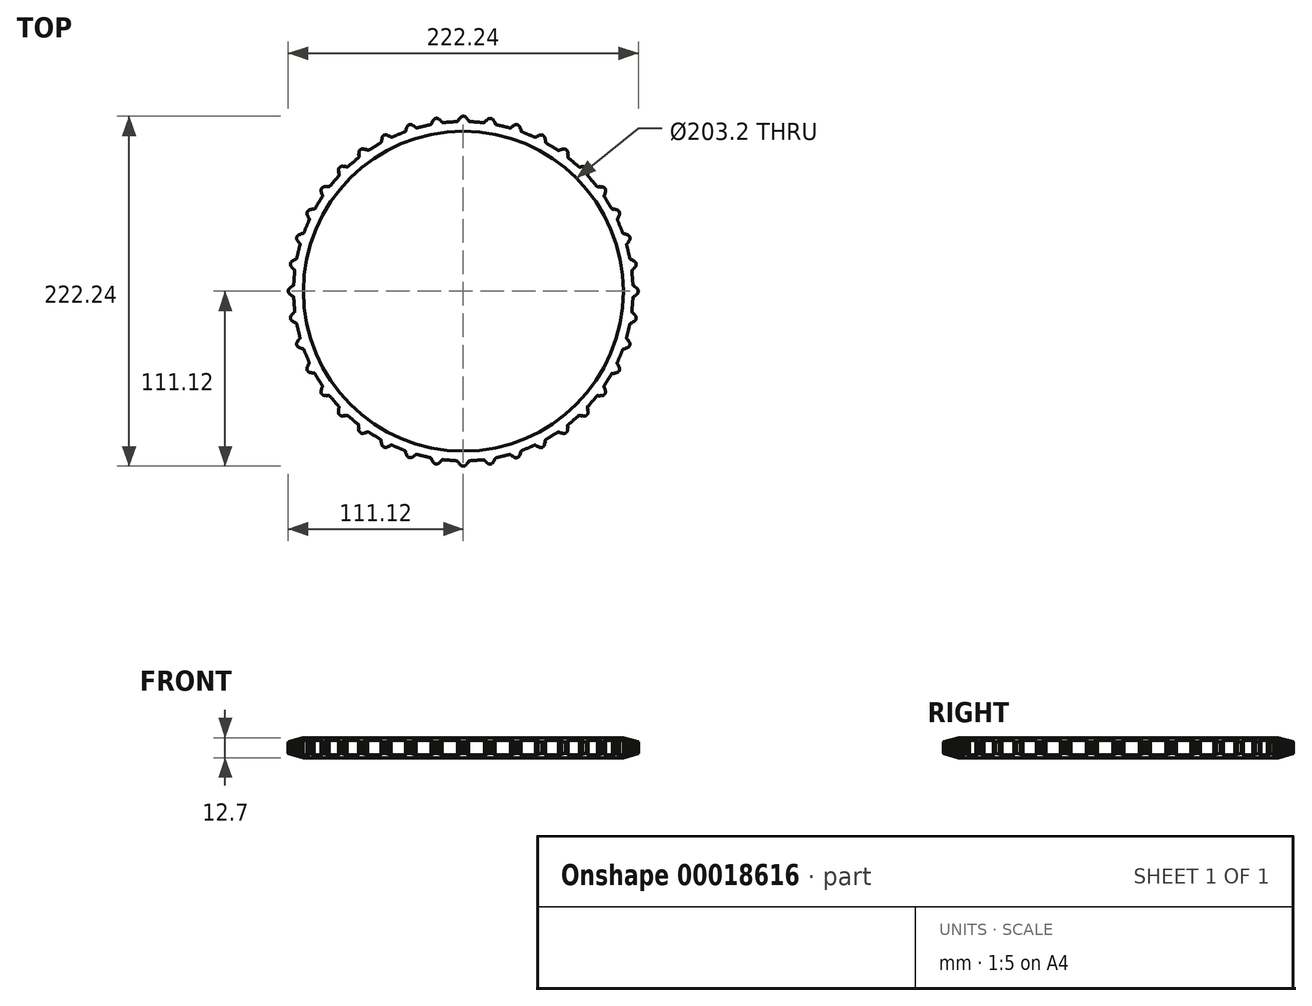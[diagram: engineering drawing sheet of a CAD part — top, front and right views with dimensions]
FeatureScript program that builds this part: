
annotation { "Feature Type Name" : "Feature", "Feature Type Description" : "" }
export const myFeature = defineFeature(function(context is Context, id is Id, definition is map)
    precondition{}
    {
        {
            var Q0;
            Q0=qCreatedBy(makeId("Top.planeOp"),FACE);
            var sketch = newSketch(context, id + "F0", { "sketchPlane" : qUnion([Q0])});
            skCircle(sketch, "E0", {"center": v(0, 0) * mm, "radius": 101.6 * mm});
            skCircle(sketch, "E1", {"center": v(0, 0) * mm, "radius": 111.13 * mm});
            skSolve(sketch);
        }
        {
            var Q0;
            Q0=qSketchRegion(id+"F0",true);
            extrude(context, id + "F1", {"entities" : qUnion([Q0]), "depth" : 12.7 * mm});
        }
        {
            var Q0;
            Q0=makeQuery(id+"F1.opExtrude","CAP_FACE",FACE,{"disambiguationData":[OSD([sQuery(id+"F0.wireOp",EDGE,"E0"),sQuery(id+"F0.wireOp",EDGE,"E1")])],"isStart":false});
            var sketch = newSketch(context, id + "F2", { "sketchPlane" : qUnion([Q0])});
            skLineSegment(sketch, "E2", {"start": v(0, 0) * mm, "end": v(0, 111.13) * mm, "construction": true});
            skArc(sketch, "E3", {"start": v(3.3, 108.7) * mm, "mid": v(2.05, 110.45) * mm, "end": v(0, 111.13) * mm});
            skCircle(sketch, "E4", {"center": v(0, 0) * mm, "radius": 107.95 * mm, "construction": true});
            skArc(sketch, "E5", {"start": v(8.83, 110.77) * mm, "mid": v(6.85, 110.27) * mm, "end": v(5.59, 108.66) * mm});
            skArc(sketch, "E6", {"start": v(3.3, 108.7) * mm, "mid": v(4.43, 107.86) * mm, "end": v(5.59, 108.66) * mm});
            skLineSegment(sketch, "E7", {"start": v(8.58, 107.6) * mm, "end": v(8.83, 110.77) * mm, "construction": true});
            skArc(sketch, "E8.1.0", {"start": v(-5.24, 108.63) * mm, "mid": v(-6.62, 110.27) * mm, "end": v(-8.72, 110.78) * mm});
            skArc(sketch, "E8.1.1", {"start": v(0.12, 111.12) * mm, "mid": v(-1.82, 110.47) * mm, "end": v(-2.96, 108.77) * mm});
            skArc(sketch, "E8.1.2", {"start": v(-5.24, 108.63) * mm, "mid": v(-4.05, 107.87) * mm, "end": v(-2.96, 108.77) * mm});
            skArc(sketch, "E8.2.0", {"start": v(-13.74, 107.88) * mm, "mid": v(-15.26, 109.41) * mm, "end": v(-17.38, 109.76) * mm});
            skArc(sketch, "E8.2.1", {"start": v(-8.6, 110.8) * mm, "mid": v(-10.48, 109.98) * mm, "end": v(-11.48, 108.2) * mm});
            skArc(sketch, "E8.2.2", {"start": v(-13.74, 107.88) * mm, "mid": v(-12.5, 107.22) * mm, "end": v(-11.48, 108.2) * mm});
            skArc(sketch, "E8.3.0", {"start": v(-22.16, 106.47) * mm, "mid": v(-23.8, 107.88) * mm, "end": v(-25.94, 108.05) * mm});
            skArc(sketch, "E8.3.1", {"start": v(-17.27, 109.77) * mm, "mid": v(-19.08, 108.82) * mm, "end": v(-19.93, 106.97) * mm});
            skArc(sketch, "E8.3.2", {"start": v(-22.16, 106.47) * mm, "mid": v(-20.87, 105.91) * mm, "end": v(-19.93, 106.97) * mm});
            skArc(sketch, "E8.4.0", {"start": v(-30.45, 104.4) * mm, "mid": v(-32.18, 105.68) * mm, "end": v(-34.34, 105.69) * mm});
            skArc(sketch, "E8.4.1", {"start": v(-25.83, 108.08) * mm, "mid": v(-27.56, 107) * mm, "end": v(-28.26, 105.07) * mm});
            skArc(sketch, "E8.4.2", {"start": v(-30.45, 104.4) * mm, "mid": v(-29.12, 103.95) * mm, "end": v(-28.26, 105.07) * mm});
            skArc(sketch, "E8.5.0", {"start": v(-38.55, 101.7) * mm, "mid": v(-40.38, 102.83) * mm, "end": v(-42.53, 102.67) * mm});
            skArc(sketch, "E8.5.1", {"start": v(-34.23, 105.72) * mm, "mid": v(-35.87, 104.5) * mm, "end": v(-36.42, 102.53) * mm});
            skArc(sketch, "E8.5.2", {"start": v(-38.55, 101.7) * mm, "mid": v(-37.18, 101.34) * mm, "end": v(-36.42, 102.53) * mm});
            skArc(sketch, "E8.6.0", {"start": v(-46.4, 98.35) * mm, "mid": v(-48.32, 99.35) * mm, "end": v(-50.45, 99.01) * mm});
            skArc(sketch, "E8.6.1", {"start": v(-42.42, 102.71) * mm, "mid": v(-43.96, 101.36) * mm, "end": v(-44.35, 99.36) * mm});
            skArc(sketch, "E8.6.2", {"start": v(-46.4, 98.35) * mm, "mid": v(-45.02, 98.12) * mm, "end": v(-44.35, 99.36) * mm});
            skArc(sketch, "E8.7.0", {"start": v(-53.98, 94.4) * mm, "mid": v(-55.97, 95.25) * mm, "end": v(-58.06, 94.75) * mm});
            skArc(sketch, "E8.7.1", {"start": v(-50.35, 99.07) * mm, "mid": v(-51.77, 97.6) * mm, "end": v(-52.01, 95.57) * mm});
            skArc(sketch, "E8.7.2", {"start": v(-53.98, 94.4) * mm, "mid": v(-52.58, 94.28) * mm, "end": v(-52.01, 95.57) * mm});
            skArc(sketch, "E8.8.0", {"start": v(-61.22, 89.88) * mm, "mid": v(-63.27, 90.56) * mm, "end": v(-65.32, 89.9) * mm});
            skArc(sketch, "E8.8.1", {"start": v(-57.96, 94.81) * mm, "mid": v(-59.27, 93.24) * mm, "end": v(-59.35, 91.2) * mm});
            skArc(sketch, "E8.8.2", {"start": v(-61.22, 89.88) * mm, "mid": v(-59.81, 89.86) * mm, "end": v(-59.35, 91.2) * mm});
            skArc(sketch, "E8.9.0", {"start": v(-68.09, 84.8) * mm, "mid": v(-70.18, 85.32) * mm, "end": v(-72.17, 84.5) * mm});
            skArc(sketch, "E8.9.1", {"start": v(-65.22, 89.97) * mm, "mid": v(-66.4, 88.3) * mm, "end": v(-66.32, 86.26) * mm});
            skArc(sketch, "E8.9.2", {"start": v(-68.09, 84.8) * mm, "mid": v(-66.68, 84.9) * mm, "end": v(-66.32, 86.26) * mm});
            skArc(sketch, "E8.10.0", {"start": v(-74.53, 79.2) * mm, "mid": v(-76.65, 79.55) * mm, "end": v(-78.58, 78.58) * mm});
            skArc(sketch, "E8.10.1", {"start": v(-72.08, 84.58) * mm, "mid": v(-73.13, 82.82) * mm, "end": v(-72.89, 80.79) * mm});
            skArc(sketch, "E8.10.2", {"start": v(-74.53, 79.2) * mm, "mid": v(-73.13, 79.4) * mm, "end": v(-72.89, 80.79) * mm});
            skArc(sketch, "E8.11.0", {"start": v(-80.51, 73.1) * mm, "mid": v(-82.66, 73.3) * mm, "end": v(-84.5, 72.17) * mm});
            skArc(sketch, "E8.11.1", {"start": v(-78.5, 78.66) * mm, "mid": v(-79.4, 76.83) * mm, "end": v(-79, 74.82) * mm});
            skArc(sketch, "E8.11.2", {"start": v(-80.51, 73.1) * mm, "mid": v(-79.14, 73.42) * mm, "end": v(-79, 74.82) * mm});
            skArc(sketch, "E8.12.0", {"start": v(-86, 66.57) * mm, "mid": v(-88.16, 66.58) * mm, "end": v(-89.9, 65.32) * mm});
            skArc(sketch, "E8.12.1", {"start": v(-84.42, 72.26) * mm, "mid": v(-85.18, 70.36) * mm, "end": v(-84.63, 68.4) * mm});
            skArc(sketch, "E8.12.2", {"start": v(-86, 66.57) * mm, "mid": v(-84.66, 66.98) * mm, "end": v(-84.63, 68.4) * mm});
            skArc(sketch, "E8.13.0", {"start": v(-90.96, 59.61) * mm, "mid": v(-93.1, 59.46) * mm, "end": v(-94.75, 58.06) * mm});
            skArc(sketch, "E8.13.1", {"start": v(-89.83, 65.41) * mm, "mid": v(-90.44, 63.46) * mm, "end": v(-89.73, 61.54) * mm});
            skArc(sketch, "E8.13.2", {"start": v(-90.96, 59.61) * mm, "mid": v(-89.65, 60.13) * mm, "end": v(-89.73, 61.54) * mm});
            skArc(sketch, "E8.14.0", {"start": v(-95.36, 52.3) * mm, "mid": v(-97.49, 51.97) * mm, "end": v(-99.01, 50.45) * mm});
            skArc(sketch, "E8.14.1", {"start": v(-94.69, 58.16) * mm, "mid": v(-95.14, 56.17) * mm, "end": v(-94.28, 54.31) * mm});
            skArc(sketch, "E8.14.2", {"start": v(-95.36, 52.3) * mm, "mid": v(-94.1, 52.92) * mm, "end": v(-94.28, 54.31) * mm});
            skArc(sketch, "E8.15.0", {"start": v(-99.16, 44.65) * mm, "mid": v(-101.26, 44.16) * mm, "end": v(-102.67, 42.53) * mm});
            skArc(sketch, "E8.15.1", {"start": v(-98.96, 50.55) * mm, "mid": v(-99.25, 48.53) * mm, "end": v(-98.25, 46.75) * mm});
            skArc(sketch, "E8.15.2", {"start": v(-99.16, 44.65) * mm, "mid": v(-97.95, 45.37) * mm, "end": v(-98.25, 46.75) * mm});
            skArc(sketch, "E8.16.0", {"start": v(-102.36, 36.73) * mm, "mid": v(-104.42, 36.08) * mm, "end": v(-105.69, 34.34) * mm});
            skArc(sketch, "E8.16.1", {"start": v(-102.62, 42.63) * mm, "mid": v(-102.76, 40.6) * mm, "end": v(-101.62, 38.9) * mm});
            skArc(sketch, "E8.16.2", {"start": v(-102.36, 36.73) * mm, "mid": v(-101.21, 37.54) * mm, "end": v(-101.62, 38.9) * mm});
            skArc(sketch, "E8.17.0", {"start": v(-104.93, 28.59) * mm, "mid": v(-106.92, 27.78) * mm, "end": v(-108.05, 25.94) * mm});
            skArc(sketch, "E8.17.1", {"start": v(-105.65, 34.45) * mm, "mid": v(-105.62, 32.4) * mm, "end": v(-104.36, 30.8) * mm});
            skArc(sketch, "E8.17.2", {"start": v(-104.93, 28.59) * mm, "mid": v(-103.84, 29.49) * mm, "end": v(-104.36, 30.8) * mm});
            skArc(sketch, "E8.18.0", {"start": v(-106.85, 20.27) * mm, "mid": v(-108.77, 19.3) * mm, "end": v(-109.76, 17.38) * mm});
            skArc(sketch, "E8.18.1", {"start": v(-108.03, 26.05) * mm, "mid": v(-107.84, 24.02) * mm, "end": v(-106.45, 22.52) * mm});
            skArc(sketch, "E8.18.2", {"start": v(-106.85, 20.27) * mm, "mid": v(-105.84, 21.25) * mm, "end": v(-106.45, 22.52) * mm});
            skArc(sketch, "E8.19.0", {"start": v(-108.1, 11.82) * mm, "mid": v(-109.95, 10.7) * mm, "end": v(-110.78, 8.72) * mm});
            skArc(sketch, "E8.19.1", {"start": v(-109.74, 17.5) * mm, "mid": v(-109.4, 15.48) * mm, "end": v(-107.9, 14.1) * mm});
            skArc(sketch, "E8.19.2", {"start": v(-108.1, 11.82) * mm, "mid": v(-107.18, 12.88) * mm, "end": v(-107.9, 14.1) * mm});
            skArc(sketch, "E8.20.0", {"start": v(-108.7, 3.3) * mm, "mid": v(-110.45, 2.05) * mm, "end": v(-111.13, 0) * mm});
            skArc(sketch, "E8.20.1", {"start": v(-110.77, 8.83) * mm, "mid": v(-110.27, 6.85) * mm, "end": v(-108.66, 5.59) * mm});
            skArc(sketch, "E8.20.2", {"start": v(-108.7, 3.3) * mm, "mid": v(-107.86, 4.43) * mm, "end": v(-108.66, 5.59) * mm});
            skArc(sketch, "E8.21.0", {"start": v(-108.63, -5.24) * mm, "mid": v(-110.27, -6.62) * mm, "end": v(-110.78, -8.72) * mm});
            skArc(sketch, "E8.21.1", {"start": v(-111.12, 0.12) * mm, "mid": v(-110.47, -1.82) * mm, "end": v(-108.77, -2.96) * mm});
            skArc(sketch, "E8.21.2", {"start": v(-108.63, -5.24) * mm, "mid": v(-107.87, -4.05) * mm, "end": v(-108.77, -2.96) * mm});
            skArc(sketch, "E8.22.0", {"start": v(-107.88, -13.74) * mm, "mid": v(-109.41, -15.26) * mm, "end": v(-109.76, -17.38) * mm});
            skArc(sketch, "E8.22.1", {"start": v(-110.8, -8.6) * mm, "mid": v(-109.98, -10.48) * mm, "end": v(-108.2, -11.48) * mm});
            skArc(sketch, "E8.22.2", {"start": v(-107.88, -13.74) * mm, "mid": v(-107.22, -12.5) * mm, "end": v(-108.2, -11.48) * mm});
            skArc(sketch, "E8.23.0", {"start": v(-106.47, -22.16) * mm, "mid": v(-107.88, -23.8) * mm, "end": v(-108.05, -25.94) * mm});
            skArc(sketch, "E8.23.1", {"start": v(-109.77, -17.27) * mm, "mid": v(-108.82, -19.08) * mm, "end": v(-106.97, -19.93) * mm});
            skArc(sketch, "E8.23.2", {"start": v(-106.47, -22.16) * mm, "mid": v(-105.91, -20.87) * mm, "end": v(-106.97, -19.93) * mm});
            skArc(sketch, "E8.24.0", {"start": v(-104.4, -30.45) * mm, "mid": v(-105.68, -32.18) * mm, "end": v(-105.69, -34.34) * mm});
            skArc(sketch, "E8.24.1", {"start": v(-108.08, -25.83) * mm, "mid": v(-107, -27.56) * mm, "end": v(-105.07, -28.26) * mm});
            skArc(sketch, "E8.24.2", {"start": v(-104.4, -30.45) * mm, "mid": v(-103.95, -29.12) * mm, "end": v(-105.07, -28.26) * mm});
            skArc(sketch, "E8.25.0", {"start": v(-101.7, -38.55) * mm, "mid": v(-102.83, -40.38) * mm, "end": v(-102.67, -42.53) * mm});
            skArc(sketch, "E8.25.1", {"start": v(-105.72, -34.23) * mm, "mid": v(-104.5, -35.87) * mm, "end": v(-102.53, -36.42) * mm});
            skArc(sketch, "E8.25.2", {"start": v(-101.7, -38.55) * mm, "mid": v(-101.34, -37.18) * mm, "end": v(-102.53, -36.42) * mm});
            skArc(sketch, "E8.26.0", {"start": v(-98.35, -46.4) * mm, "mid": v(-99.35, -48.32) * mm, "end": v(-99.01, -50.45) * mm});
            skArc(sketch, "E8.26.1", {"start": v(-102.71, -42.42) * mm, "mid": v(-101.36, -43.96) * mm, "end": v(-99.36, -44.35) * mm});
            skArc(sketch, "E8.26.2", {"start": v(-98.35, -46.4) * mm, "mid": v(-98.12, -45.02) * mm, "end": v(-99.36, -44.35) * mm});
            skArc(sketch, "E8.27.0", {"start": v(-94.4, -53.98) * mm, "mid": v(-95.25, -55.97) * mm, "end": v(-94.75, -58.06) * mm});
            skArc(sketch, "E8.27.1", {"start": v(-99.07, -50.35) * mm, "mid": v(-97.6, -51.77) * mm, "end": v(-95.57, -52.01) * mm});
            skArc(sketch, "E8.27.2", {"start": v(-94.4, -53.98) * mm, "mid": v(-94.28, -52.58) * mm, "end": v(-95.57, -52.01) * mm});
            skArc(sketch, "E8.28.0", {"start": v(-89.88, -61.22) * mm, "mid": v(-90.56, -63.27) * mm, "end": v(-89.9, -65.32) * mm});
            skArc(sketch, "E8.28.1", {"start": v(-94.81, -57.96) * mm, "mid": v(-93.24, -59.27) * mm, "end": v(-91.2, -59.35) * mm});
            skArc(sketch, "E8.28.2", {"start": v(-89.88, -61.22) * mm, "mid": v(-89.86, -59.81) * mm, "end": v(-91.2, -59.35) * mm});
            skArc(sketch, "E8.29.0", {"start": v(-84.8, -68.09) * mm, "mid": v(-85.32, -70.18) * mm, "end": v(-84.5, -72.17) * mm});
            skArc(sketch, "E8.29.1", {"start": v(-89.97, -65.22) * mm, "mid": v(-88.3, -66.4) * mm, "end": v(-86.26, -66.32) * mm});
            skArc(sketch, "E8.29.2", {"start": v(-84.8, -68.09) * mm, "mid": v(-84.9, -66.68) * mm, "end": v(-86.26, -66.32) * mm});
            skArc(sketch, "E8.30.0", {"start": v(-79.2, -74.53) * mm, "mid": v(-79.55, -76.65) * mm, "end": v(-78.58, -78.58) * mm});
            skArc(sketch, "E8.30.1", {"start": v(-84.58, -72.08) * mm, "mid": v(-82.82, -73.13) * mm, "end": v(-80.79, -72.89) * mm});
            skArc(sketch, "E8.30.2", {"start": v(-79.2, -74.53) * mm, "mid": v(-79.4, -73.13) * mm, "end": v(-80.79, -72.89) * mm});
            skArc(sketch, "E8.31.0", {"start": v(-73.1, -80.51) * mm, "mid": v(-73.3, -82.66) * mm, "end": v(-72.17, -84.5) * mm});
            skArc(sketch, "E8.31.1", {"start": v(-78.66, -78.5) * mm, "mid": v(-76.83, -79.4) * mm, "end": v(-74.82, -79) * mm});
            skArc(sketch, "E8.31.2", {"start": v(-73.1, -80.51) * mm, "mid": v(-73.42, -79.14) * mm, "end": v(-74.82, -79) * mm});
            skArc(sketch, "E8.32.0", {"start": v(-66.57, -86) * mm, "mid": v(-66.58, -88.16) * mm, "end": v(-65.32, -89.9) * mm});
            skArc(sketch, "E8.32.1", {"start": v(-72.26, -84.42) * mm, "mid": v(-70.36, -85.18) * mm, "end": v(-68.4, -84.63) * mm});
            skArc(sketch, "E8.32.2", {"start": v(-66.57, -86) * mm, "mid": v(-66.98, -84.66) * mm, "end": v(-68.4, -84.63) * mm});
            skArc(sketch, "E8.33.0", {"start": v(-59.61, -90.96) * mm, "mid": v(-59.46, -93.1) * mm, "end": v(-58.06, -94.75) * mm});
            skArc(sketch, "E8.33.1", {"start": v(-65.41, -89.83) * mm, "mid": v(-63.46, -90.44) * mm, "end": v(-61.54, -89.73) * mm});
            skArc(sketch, "E8.33.2", {"start": v(-59.61, -90.96) * mm, "mid": v(-60.13, -89.65) * mm, "end": v(-61.54, -89.73) * mm});
            skArc(sketch, "E8.34.0", {"start": v(-52.3, -95.36) * mm, "mid": v(-51.97, -97.49) * mm, "end": v(-50.45, -99.01) * mm});
            skArc(sketch, "E8.34.1", {"start": v(-58.16, -94.69) * mm, "mid": v(-56.17, -95.14) * mm, "end": v(-54.31, -94.28) * mm});
            skArc(sketch, "E8.34.2", {"start": v(-52.3, -95.36) * mm, "mid": v(-52.92, -94.1) * mm, "end": v(-54.31, -94.28) * mm});
            skArc(sketch, "E8.35.0", {"start": v(-44.65, -99.16) * mm, "mid": v(-44.16, -101.26) * mm, "end": v(-42.53, -102.67) * mm});
            skArc(sketch, "E8.35.1", {"start": v(-50.55, -98.96) * mm, "mid": v(-48.53, -99.25) * mm, "end": v(-46.75, -98.25) * mm});
            skArc(sketch, "E8.35.2", {"start": v(-44.65, -99.16) * mm, "mid": v(-45.37, -97.95) * mm, "end": v(-46.75, -98.25) * mm});
            skArc(sketch, "E8.36.0", {"start": v(-36.73, -102.36) * mm, "mid": v(-36.08, -104.42) * mm, "end": v(-34.34, -105.69) * mm});
            skArc(sketch, "E8.36.1", {"start": v(-42.63, -102.62) * mm, "mid": v(-40.6, -102.76) * mm, "end": v(-38.9, -101.62) * mm});
            skArc(sketch, "E8.36.2", {"start": v(-36.73, -102.36) * mm, "mid": v(-37.54, -101.21) * mm, "end": v(-38.9, -101.62) * mm});
            skArc(sketch, "E8.37.0", {"start": v(-28.59, -104.93) * mm, "mid": v(-27.78, -106.92) * mm, "end": v(-25.94, -108.05) * mm});
            skArc(sketch, "E8.37.1", {"start": v(-34.45, -105.65) * mm, "mid": v(-32.4, -105.62) * mm, "end": v(-30.8, -104.36) * mm});
            skArc(sketch, "E8.37.2", {"start": v(-28.59, -104.93) * mm, "mid": v(-29.49, -103.84) * mm, "end": v(-30.8, -104.36) * mm});
            skArc(sketch, "E8.38.0", {"start": v(-20.27, -106.85) * mm, "mid": v(-19.3, -108.77) * mm, "end": v(-17.38, -109.76) * mm});
            skArc(sketch, "E8.38.1", {"start": v(-26.05, -108.03) * mm, "mid": v(-24.02, -107.84) * mm, "end": v(-22.52, -106.45) * mm});
            skArc(sketch, "E8.38.2", {"start": v(-20.27, -106.85) * mm, "mid": v(-21.25, -105.84) * mm, "end": v(-22.52, -106.45) * mm});
            skArc(sketch, "E8.39.0", {"start": v(-11.82, -108.1) * mm, "mid": v(-10.7, -109.95) * mm, "end": v(-8.72, -110.78) * mm});
            skArc(sketch, "E8.39.1", {"start": v(-17.5, -109.74) * mm, "mid": v(-15.48, -109.4) * mm, "end": v(-14.1, -107.9) * mm});
            skArc(sketch, "E8.39.2", {"start": v(-11.82, -108.1) * mm, "mid": v(-12.88, -107.18) * mm, "end": v(-14.1, -107.9) * mm});
            skArc(sketch, "E8.40.0", {"start": v(-3.3, -108.7) * mm, "mid": v(-2.05, -110.45) * mm, "end": v(0, -111.13) * mm});
            skArc(sketch, "E8.40.1", {"start": v(-8.83, -110.77) * mm, "mid": v(-6.85, -110.27) * mm, "end": v(-5.59, -108.66) * mm});
            skArc(sketch, "E8.40.2", {"start": v(-3.3, -108.7) * mm, "mid": v(-4.43, -107.86) * mm, "end": v(-5.59, -108.66) * mm});
            skArc(sketch, "E8.41.0", {"start": v(5.24, -108.63) * mm, "mid": v(6.62, -110.27) * mm, "end": v(8.72, -110.78) * mm});
            skArc(sketch, "E8.41.1", {"start": v(-0.12, -111.12) * mm, "mid": v(1.82, -110.47) * mm, "end": v(2.96, -108.77) * mm});
            skArc(sketch, "E8.41.2", {"start": v(5.24, -108.63) * mm, "mid": v(4.05, -107.87) * mm, "end": v(2.96, -108.77) * mm});
            skArc(sketch, "E8.42.0", {"start": v(13.74, -107.88) * mm, "mid": v(15.26, -109.41) * mm, "end": v(17.38, -109.76) * mm});
            skArc(sketch, "E8.42.1", {"start": v(8.6, -110.8) * mm, "mid": v(10.48, -109.98) * mm, "end": v(11.48, -108.2) * mm});
            skArc(sketch, "E8.42.2", {"start": v(13.74, -107.88) * mm, "mid": v(12.5, -107.22) * mm, "end": v(11.48, -108.2) * mm});
            skArc(sketch, "E8.43.0", {"start": v(22.16, -106.47) * mm, "mid": v(23.8, -107.88) * mm, "end": v(25.94, -108.05) * mm});
            skArc(sketch, "E8.43.1", {"start": v(17.27, -109.77) * mm, "mid": v(19.08, -108.82) * mm, "end": v(19.93, -106.97) * mm});
            skArc(sketch, "E8.43.2", {"start": v(22.16, -106.47) * mm, "mid": v(20.87, -105.91) * mm, "end": v(19.93, -106.97) * mm});
            skArc(sketch, "E8.44.0", {"start": v(30.45, -104.4) * mm, "mid": v(32.18, -105.68) * mm, "end": v(34.34, -105.69) * mm});
            skArc(sketch, "E8.44.1", {"start": v(25.83, -108.08) * mm, "mid": v(27.56, -107) * mm, "end": v(28.26, -105.07) * mm});
            skArc(sketch, "E8.44.2", {"start": v(30.45, -104.4) * mm, "mid": v(29.12, -103.95) * mm, "end": v(28.26, -105.07) * mm});
            skArc(sketch, "E8.45.0", {"start": v(38.55, -101.7) * mm, "mid": v(40.38, -102.83) * mm, "end": v(42.53, -102.67) * mm});
            skArc(sketch, "E8.45.1", {"start": v(34.23, -105.72) * mm, "mid": v(35.87, -104.5) * mm, "end": v(36.42, -102.53) * mm});
            skArc(sketch, "E8.45.2", {"start": v(38.55, -101.7) * mm, "mid": v(37.18, -101.34) * mm, "end": v(36.42, -102.53) * mm});
            skArc(sketch, "E8.46.0", {"start": v(46.4, -98.35) * mm, "mid": v(48.32, -99.35) * mm, "end": v(50.45, -99.01) * mm});
            skArc(sketch, "E8.46.1", {"start": v(42.42, -102.71) * mm, "mid": v(43.96, -101.36) * mm, "end": v(44.35, -99.36) * mm});
            skArc(sketch, "E8.46.2", {"start": v(46.4, -98.35) * mm, "mid": v(45.02, -98.12) * mm, "end": v(44.35, -99.36) * mm});
            skArc(sketch, "E8.47.0", {"start": v(53.98, -94.4) * mm, "mid": v(55.97, -95.25) * mm, "end": v(58.06, -94.75) * mm});
            skArc(sketch, "E8.47.1", {"start": v(50.35, -99.07) * mm, "mid": v(51.77, -97.6) * mm, "end": v(52.01, -95.57) * mm});
            skArc(sketch, "E8.47.2", {"start": v(53.98, -94.4) * mm, "mid": v(52.58, -94.28) * mm, "end": v(52.01, -95.57) * mm});
            skArc(sketch, "E8.48.0", {"start": v(61.22, -89.88) * mm, "mid": v(63.27, -90.56) * mm, "end": v(65.32, -89.9) * mm});
            skArc(sketch, "E8.48.1", {"start": v(57.96, -94.81) * mm, "mid": v(59.27, -93.24) * mm, "end": v(59.35, -91.2) * mm});
            skArc(sketch, "E8.48.2", {"start": v(61.22, -89.88) * mm, "mid": v(59.81, -89.86) * mm, "end": v(59.35, -91.2) * mm});
            skArc(sketch, "E8.49.0", {"start": v(68.09, -84.8) * mm, "mid": v(70.18, -85.32) * mm, "end": v(72.17, -84.5) * mm});
            skArc(sketch, "E8.49.1", {"start": v(65.22, -89.97) * mm, "mid": v(66.4, -88.3) * mm, "end": v(66.32, -86.26) * mm});
            skArc(sketch, "E8.49.2", {"start": v(68.09, -84.8) * mm, "mid": v(66.68, -84.9) * mm, "end": v(66.32, -86.26) * mm});
            skArc(sketch, "E8.50.0", {"start": v(74.53, -79.2) * mm, "mid": v(76.65, -79.55) * mm, "end": v(78.58, -78.58) * mm});
            skArc(sketch, "E8.50.1", {"start": v(72.08, -84.58) * mm, "mid": v(73.13, -82.82) * mm, "end": v(72.89, -80.79) * mm});
            skArc(sketch, "E8.50.2", {"start": v(74.53, -79.2) * mm, "mid": v(73.13, -79.4) * mm, "end": v(72.89, -80.79) * mm});
            skArc(sketch, "E8.51.0", {"start": v(80.51, -73.1) * mm, "mid": v(82.66, -73.3) * mm, "end": v(84.5, -72.17) * mm});
            skArc(sketch, "E8.51.1", {"start": v(78.5, -78.66) * mm, "mid": v(79.4, -76.83) * mm, "end": v(79, -74.82) * mm});
            skArc(sketch, "E8.51.2", {"start": v(80.51, -73.1) * mm, "mid": v(79.14, -73.42) * mm, "end": v(79, -74.82) * mm});
            skArc(sketch, "E8.52.0", {"start": v(86, -66.57) * mm, "mid": v(88.16, -66.58) * mm, "end": v(89.9, -65.32) * mm});
            skArc(sketch, "E8.52.1", {"start": v(84.42, -72.26) * mm, "mid": v(85.18, -70.36) * mm, "end": v(84.63, -68.4) * mm});
            skArc(sketch, "E8.52.2", {"start": v(86, -66.57) * mm, "mid": v(84.66, -66.98) * mm, "end": v(84.63, -68.4) * mm});
            skArc(sketch, "E8.53.0", {"start": v(90.96, -59.61) * mm, "mid": v(93.1, -59.46) * mm, "end": v(94.75, -58.06) * mm});
            skArc(sketch, "E8.53.1", {"start": v(89.83, -65.41) * mm, "mid": v(90.44, -63.46) * mm, "end": v(89.73, -61.54) * mm});
            skArc(sketch, "E8.53.2", {"start": v(90.96, -59.61) * mm, "mid": v(89.65, -60.13) * mm, "end": v(89.73, -61.54) * mm});
            skArc(sketch, "E8.54.0", {"start": v(95.36, -52.3) * mm, "mid": v(97.49, -51.97) * mm, "end": v(99.01, -50.45) * mm});
            skArc(sketch, "E8.54.1", {"start": v(94.69, -58.16) * mm, "mid": v(95.14, -56.17) * mm, "end": v(94.28, -54.31) * mm});
            skArc(sketch, "E8.54.2", {"start": v(95.36, -52.3) * mm, "mid": v(94.1, -52.92) * mm, "end": v(94.28, -54.31) * mm});
            skArc(sketch, "E8.55.0", {"start": v(99.16, -44.65) * mm, "mid": v(101.26, -44.16) * mm, "end": v(102.67, -42.53) * mm});
            skArc(sketch, "E8.55.1", {"start": v(98.96, -50.55) * mm, "mid": v(99.25, -48.53) * mm, "end": v(98.25, -46.75) * mm});
            skArc(sketch, "E8.55.2", {"start": v(99.16, -44.65) * mm, "mid": v(97.95, -45.37) * mm, "end": v(98.25, -46.75) * mm});
            skArc(sketch, "E8.56.0", {"start": v(102.36, -36.73) * mm, "mid": v(104.42, -36.08) * mm, "end": v(105.69, -34.34) * mm});
            skArc(sketch, "E8.56.1", {"start": v(102.62, -42.63) * mm, "mid": v(102.76, -40.6) * mm, "end": v(101.62, -38.9) * mm});
            skArc(sketch, "E8.56.2", {"start": v(102.36, -36.73) * mm, "mid": v(101.21, -37.54) * mm, "end": v(101.62, -38.9) * mm});
            skArc(sketch, "E8.57.0", {"start": v(104.93, -28.59) * mm, "mid": v(106.92, -27.78) * mm, "end": v(108.05, -25.94) * mm});
            skArc(sketch, "E8.57.1", {"start": v(105.65, -34.45) * mm, "mid": v(105.62, -32.4) * mm, "end": v(104.36, -30.8) * mm});
            skArc(sketch, "E8.57.2", {"start": v(104.93, -28.59) * mm, "mid": v(103.84, -29.49) * mm, "end": v(104.36, -30.8) * mm});
            skArc(sketch, "E8.58.0", {"start": v(106.85, -20.27) * mm, "mid": v(108.77, -19.3) * mm, "end": v(109.76, -17.38) * mm});
            skArc(sketch, "E8.58.1", {"start": v(108.03, -26.05) * mm, "mid": v(107.84, -24.02) * mm, "end": v(106.45, -22.52) * mm});
            skArc(sketch, "E8.58.2", {"start": v(106.85, -20.27) * mm, "mid": v(105.84, -21.25) * mm, "end": v(106.45, -22.52) * mm});
            skArc(sketch, "E8.59.0", {"start": v(108.1, -11.82) * mm, "mid": v(109.95, -10.7) * mm, "end": v(110.78, -8.72) * mm});
            skArc(sketch, "E8.59.1", {"start": v(109.74, -17.5) * mm, "mid": v(109.4, -15.48) * mm, "end": v(107.9, -14.1) * mm});
            skArc(sketch, "E8.59.2", {"start": v(108.1, -11.82) * mm, "mid": v(107.18, -12.88) * mm, "end": v(107.9, -14.1) * mm});
            skArc(sketch, "E8.60.0", {"start": v(108.7, -3.3) * mm, "mid": v(110.45, -2.05) * mm, "end": v(111.13, 0) * mm});
            skArc(sketch, "E8.60.1", {"start": v(110.77, -8.83) * mm, "mid": v(110.27, -6.85) * mm, "end": v(108.66, -5.59) * mm});
            skArc(sketch, "E8.60.2", {"start": v(108.7, -3.3) * mm, "mid": v(107.86, -4.43) * mm, "end": v(108.66, -5.59) * mm});
            skArc(sketch, "E8.61.0", {"start": v(108.63, 5.24) * mm, "mid": v(110.27, 6.62) * mm, "end": v(110.78, 8.72) * mm});
            skArc(sketch, "E8.61.1", {"start": v(111.12, -0.12) * mm, "mid": v(110.47, 1.82) * mm, "end": v(108.77, 2.96) * mm});
            skArc(sketch, "E8.61.2", {"start": v(108.63, 5.24) * mm, "mid": v(107.87, 4.05) * mm, "end": v(108.77, 2.96) * mm});
            skArc(sketch, "E8.62.0", {"start": v(107.88, 13.74) * mm, "mid": v(109.41, 15.26) * mm, "end": v(109.76, 17.38) * mm});
            skArc(sketch, "E8.62.1", {"start": v(110.8, 8.6) * mm, "mid": v(109.98, 10.48) * mm, "end": v(108.2, 11.48) * mm});
            skArc(sketch, "E8.62.2", {"start": v(107.88, 13.74) * mm, "mid": v(107.22, 12.5) * mm, "end": v(108.2, 11.48) * mm});
            skArc(sketch, "E8.63.0", {"start": v(106.47, 22.16) * mm, "mid": v(107.88, 23.8) * mm, "end": v(108.05, 25.94) * mm});
            skArc(sketch, "E8.63.1", {"start": v(109.77, 17.27) * mm, "mid": v(108.82, 19.08) * mm, "end": v(106.97, 19.93) * mm});
            skArc(sketch, "E8.63.2", {"start": v(106.47, 22.16) * mm, "mid": v(105.91, 20.87) * mm, "end": v(106.97, 19.93) * mm});
            skArc(sketch, "E8.64.0", {"start": v(104.4, 30.45) * mm, "mid": v(105.68, 32.18) * mm, "end": v(105.69, 34.34) * mm});
            skArc(sketch, "E8.64.1", {"start": v(108.08, 25.83) * mm, "mid": v(107, 27.56) * mm, "end": v(105.07, 28.26) * mm});
            skArc(sketch, "E8.64.2", {"start": v(104.4, 30.45) * mm, "mid": v(103.95, 29.12) * mm, "end": v(105.07, 28.26) * mm});
            skArc(sketch, "E8.65.0", {"start": v(101.7, 38.55) * mm, "mid": v(102.83, 40.38) * mm, "end": v(102.67, 42.53) * mm});
            skArc(sketch, "E8.65.1", {"start": v(105.72, 34.23) * mm, "mid": v(104.5, 35.87) * mm, "end": v(102.53, 36.42) * mm});
            skArc(sketch, "E8.65.2", {"start": v(101.7, 38.55) * mm, "mid": v(101.34, 37.18) * mm, "end": v(102.53, 36.42) * mm});
            skArc(sketch, "E8.66.0", {"start": v(98.35, 46.4) * mm, "mid": v(99.35, 48.32) * mm, "end": v(99.01, 50.45) * mm});
            skArc(sketch, "E8.66.1", {"start": v(102.71, 42.42) * mm, "mid": v(101.36, 43.96) * mm, "end": v(99.36, 44.35) * mm});
            skArc(sketch, "E8.66.2", {"start": v(98.35, 46.4) * mm, "mid": v(98.12, 45.02) * mm, "end": v(99.36, 44.35) * mm});
            skArc(sketch, "E8.67.0", {"start": v(94.4, 53.98) * mm, "mid": v(95.25, 55.97) * mm, "end": v(94.75, 58.06) * mm});
            skArc(sketch, "E8.67.1", {"start": v(99.07, 50.35) * mm, "mid": v(97.6, 51.77) * mm, "end": v(95.57, 52.01) * mm});
            skArc(sketch, "E8.67.2", {"start": v(94.4, 53.98) * mm, "mid": v(94.28, 52.58) * mm, "end": v(95.57, 52.01) * mm});
            skArc(sketch, "E8.68.0", {"start": v(89.88, 61.22) * mm, "mid": v(90.56, 63.27) * mm, "end": v(89.9, 65.32) * mm});
            skArc(sketch, "E8.68.1", {"start": v(94.81, 57.96) * mm, "mid": v(93.24, 59.27) * mm, "end": v(91.2, 59.35) * mm});
            skArc(sketch, "E8.68.2", {"start": v(89.88, 61.22) * mm, "mid": v(89.86, 59.81) * mm, "end": v(91.2, 59.35) * mm});
            skArc(sketch, "E8.69.0", {"start": v(84.8, 68.09) * mm, "mid": v(85.32, 70.18) * mm, "end": v(84.5, 72.17) * mm});
            skArc(sketch, "E8.69.1", {"start": v(89.97, 65.22) * mm, "mid": v(88.3, 66.4) * mm, "end": v(86.26, 66.32) * mm});
            skArc(sketch, "E8.69.2", {"start": v(84.8, 68.09) * mm, "mid": v(84.9, 66.68) * mm, "end": v(86.26, 66.32) * mm});
            skArc(sketch, "E8.70.0", {"start": v(79.2, 74.53) * mm, "mid": v(79.55, 76.65) * mm, "end": v(78.58, 78.58) * mm});
            skArc(sketch, "E8.70.1", {"start": v(84.58, 72.08) * mm, "mid": v(82.82, 73.13) * mm, "end": v(80.79, 72.89) * mm});
            skArc(sketch, "E8.70.2", {"start": v(79.2, 74.53) * mm, "mid": v(79.4, 73.13) * mm, "end": v(80.79, 72.89) * mm});
            skArc(sketch, "E8.71.0", {"start": v(73.1, 80.51) * mm, "mid": v(73.3, 82.66) * mm, "end": v(72.17, 84.5) * mm});
            skArc(sketch, "E8.71.1", {"start": v(78.66, 78.5) * mm, "mid": v(76.83, 79.4) * mm, "end": v(74.82, 79) * mm});
            skArc(sketch, "E8.71.2", {"start": v(73.1, 80.51) * mm, "mid": v(73.42, 79.14) * mm, "end": v(74.82, 79) * mm});
            skArc(sketch, "E8.72.0", {"start": v(66.57, 86) * mm, "mid": v(66.58, 88.16) * mm, "end": v(65.32, 89.9) * mm});
            skArc(sketch, "E8.72.1", {"start": v(72.26, 84.42) * mm, "mid": v(70.36, 85.18) * mm, "end": v(68.4, 84.63) * mm});
            skArc(sketch, "E8.72.2", {"start": v(66.57, 86) * mm, "mid": v(66.98, 84.66) * mm, "end": v(68.4, 84.63) * mm});
            skArc(sketch, "E8.73.0", {"start": v(59.61, 90.96) * mm, "mid": v(59.46, 93.1) * mm, "end": v(58.06, 94.75) * mm});
            skArc(sketch, "E8.73.1", {"start": v(65.41, 89.83) * mm, "mid": v(63.46, 90.44) * mm, "end": v(61.54, 89.73) * mm});
            skArc(sketch, "E8.73.2", {"start": v(59.61, 90.96) * mm, "mid": v(60.13, 89.65) * mm, "end": v(61.54, 89.73) * mm});
            skArc(sketch, "E8.74.0", {"start": v(52.3, 95.36) * mm, "mid": v(51.97, 97.49) * mm, "end": v(50.45, 99.01) * mm});
            skArc(sketch, "E8.74.1", {"start": v(58.16, 94.69) * mm, "mid": v(56.17, 95.14) * mm, "end": v(54.31, 94.28) * mm});
            skArc(sketch, "E8.74.2", {"start": v(52.3, 95.36) * mm, "mid": v(52.92, 94.1) * mm, "end": v(54.31, 94.28) * mm});
            skArc(sketch, "E8.75.0", {"start": v(44.65, 99.16) * mm, "mid": v(44.16, 101.26) * mm, "end": v(42.53, 102.67) * mm});
            skArc(sketch, "E8.75.1", {"start": v(50.55, 98.96) * mm, "mid": v(48.53, 99.25) * mm, "end": v(46.75, 98.25) * mm});
            skArc(sketch, "E8.75.2", {"start": v(44.65, 99.16) * mm, "mid": v(45.37, 97.95) * mm, "end": v(46.75, 98.25) * mm});
            skArc(sketch, "E8.76.0", {"start": v(36.73, 102.36) * mm, "mid": v(36.08, 104.42) * mm, "end": v(34.34, 105.69) * mm});
            skArc(sketch, "E8.76.1", {"start": v(42.63, 102.62) * mm, "mid": v(40.6, 102.76) * mm, "end": v(38.9, 101.62) * mm});
            skArc(sketch, "E8.76.2", {"start": v(36.73, 102.36) * mm, "mid": v(37.54, 101.21) * mm, "end": v(38.9, 101.62) * mm});
            skArc(sketch, "E8.77.0", {"start": v(28.59, 104.93) * mm, "mid": v(27.78, 106.92) * mm, "end": v(25.94, 108.05) * mm});
            skArc(sketch, "E8.77.1", {"start": v(34.45, 105.65) * mm, "mid": v(32.4, 105.62) * mm, "end": v(30.8, 104.36) * mm});
            skArc(sketch, "E8.77.2", {"start": v(28.59, 104.93) * mm, "mid": v(29.49, 103.84) * mm, "end": v(30.8, 104.36) * mm});
            skArc(sketch, "E8.78.0", {"start": v(20.27, 106.85) * mm, "mid": v(19.3, 108.77) * mm, "end": v(17.38, 109.76) * mm});
            skArc(sketch, "E8.78.1", {"start": v(26.05, 108.03) * mm, "mid": v(24.02, 107.84) * mm, "end": v(22.52, 106.45) * mm});
            skArc(sketch, "E8.78.2", {"start": v(20.27, 106.85) * mm, "mid": v(21.25, 105.84) * mm, "end": v(22.52, 106.45) * mm});
            skArc(sketch, "E8.79.0", {"start": v(11.82, 108.1) * mm, "mid": v(10.7, 109.95) * mm, "end": v(8.72, 110.78) * mm});
            skArc(sketch, "E8.79.1", {"start": v(17.5, 109.74) * mm, "mid": v(15.48, 109.4) * mm, "end": v(14.1, 107.9) * mm});
            skArc(sketch, "E8.79.2", {"start": v(11.82, 108.1) * mm, "mid": v(12.88, 107.18) * mm, "end": v(14.1, 107.9) * mm});
            skCircle(sketch, "E9", {"center": v(0, 0) * mm, "radius": 129.3 * mm});
            skSolve(sketch);
        }
        {
            var Q0;
            Q0=qSketchRegion(id+"F2",true);
            extrude(context, id + "F3", {"entities" : qUnion([Q0]), "operationType" : NewBodyOperationType.REMOVE, "oppositeDirection" : true, "depth" : 25.4 * mm});
        }
        {
            var Q0;
            Q0=qCreatedBy(makeId("Top.planeOp"),FACE);
            var sketch = newSketch(context, id + "F4", { "sketchPlane" : qUnion([Q0])});
            skCircle(sketch, "E10", {"center": v(0, 0) * mm, "radius": 106.71 * mm});
            skSolve(sketch);
        }
        {
            var Q0;
            Q0=qSketchRegion(id+"F4",true);
            extrude(context, id + "F5", {"entities" : qUnion([Q0]), "depth" : 19.05 * mm, "hasSecondDirection" : true, "secondDirectionOppositeDirection" : true, "secondDirectionDepth" : 6.35 * mm});
        }
        {
            var Q0;
            Q0=makeQuery(id+"F5.opExtrude","CAP_EDGE",EDGE,{"disambiguationData":[OSD([sQuery(id+"F4.wireOp",EDGE,"E10")])],"isStart":false});
            var Q1;
            Q1=makeQuery(id+"F5.opExtrude","CAP_EDGE",EDGE,{"disambiguationData":[OSD([sQuery(id+"F4.wireOp",EDGE,"E10")])],"isStart":true});
            fillet(context, id + "F6", {"entities" : qUnion([Q0, Q1]), "radius" : 6.35 * mm, "tangentPropagation" : true, "allowEdgeOverflow" : false});
        }
        {
            var Q0;
            Q0=makeQuery(id+"F5.opExtrude","CAP_FACE",FACE,{"disambiguationData":[OSD([sQuery(id+"F4.wireOp",EDGE,"E10")])],"isStart":false});
            var sketch = newSketch(context, id + "F7", { "sketchPlane" : qUnion([Q0])});
            skArc(sketch, "E11", {"start": v(-85.48, 42.02) * mm, "mid": v(-95.25, 0) * mm, "end": v(-85.48, -42.02) * mm});
            skLineSegment(sketch, "E12.rect.left", {"start": v(6.35, 95.04) * mm, "end": v(6.35, 17.96) * mm});
            skLineSegment(sketch, "E12.rect.right", {"start": v(-6.35, 95.04) * mm, "end": v(-6.35, 17.96) * mm});
            skPoint(sketch, "E12.rect.top.end.orphan", {"position": v(-6.35, -100.16) * mm});
            skPoint(sketch, "E13.trimOffspring.end.orphan", {"position": v(6.35, -100.16) * mm});
            skPoint(sketch, "E14.orphan", {"position": v(6.35, 100.16) * mm});
            skPoint(sketch, "E15.orphan", {"position": v(-6.35, 100.16) * mm});
            skLineSegment(sketch, "E16.1.0", {"start": v(-85.48, 42.02) * mm, "end": v(-18.73, 3.48) * mm});
            skLineSegment(sketch, "E16.1.2", {"start": v(-79.13, 53.02) * mm, "end": v(-12.38, 14.48) * mm});
            skPoint(sketch, "E16.1.3", {"position": v(-89.92, 44.58) * mm});
            skPoint(sketch, "E16.1.4", {"position": v(-83.57, 55.58) * mm});
            skLineSegment(sketch, "E16.2.0", {"start": v(-79.13, -53.02) * mm, "end": v(-12.38, -14.48) * mm});
            skLineSegment(sketch, "E16.2.2", {"start": v(-85.48, -42.02) * mm, "end": v(-18.73, -3.48) * mm});
            skPoint(sketch, "E16.2.3", {"position": v(-83.57, -55.58) * mm});
            skPoint(sketch, "E16.2.4", {"position": v(-89.92, -44.58) * mm});
            skLineSegment(sketch, "E16.3.0", {"start": v(6.35, -95.04) * mm, "end": v(6.35, -17.96) * mm});
            skLineSegment(sketch, "E16.3.2", {"start": v(-6.35, -95.04) * mm, "end": v(-6.35, -17.96) * mm});
            skLineSegment(sketch, "E16.4.0", {"start": v(85.48, -42.02) * mm, "end": v(18.73, -3.48) * mm});
            skLineSegment(sketch, "E16.4.2", {"start": v(79.13, -53.02) * mm, "end": v(12.38, -14.48) * mm});
            skPoint(sketch, "E16.4.3", {"position": v(89.92, -44.58) * mm});
            skPoint(sketch, "E16.4.4", {"position": v(83.57, -55.58) * mm});
            skLineSegment(sketch, "E16.5.0", {"start": v(79.13, 53.02) * mm, "end": v(12.38, 14.48) * mm});
            skLineSegment(sketch, "E16.5.2", {"start": v(85.48, 42.02) * mm, "end": v(18.73, 3.48) * mm});
            skPoint(sketch, "E16.5.3", {"position": v(83.57, 55.58) * mm});
            skPoint(sketch, "E16.5.4", {"position": v(89.92, 44.58) * mm});
            skArc(sketch, "E17", {"start": v(-12.38, -14.48) * mm, "mid": v(-9.52, -16.5) * mm, "end": v(-6.35, -17.96) * mm});
            skArc(sketch, "E18.trimOffspring", {"start": v(-6.35, 95.04) * mm, "mid": v(-47.62, 82.49) * mm, "end": v(-79.13, 53.02) * mm});
            skArc(sketch, "E19.trimOffspring", {"start": v(79.13, 53.02) * mm, "mid": v(47.63, 82.49) * mm, "end": v(6.35, 95.04) * mm});
            skArc(sketch, "E20.trimOffspring", {"start": v(85.48, -42.02) * mm, "mid": v(95.25, 0) * mm, "end": v(85.48, 42.02) * mm});
            skArc(sketch, "E21.trimOffspring", {"start": v(6.35, -95.04) * mm, "mid": v(47.62, -82.49) * mm, "end": v(79.13, -53.02) * mm});
            skArc(sketch, "E22.trimOffspring", {"start": v(-79.13, -53.02) * mm, "mid": v(-47.63, -82.49) * mm, "end": v(-6.35, -95.04) * mm});
            skPoint(sketch, "E23.trimOffspring.end.orphan", {"position": v(-6.35, 0) * mm});
            skPoint(sketch, "E24.orphan", {"position": v(3.18, 5.5) * mm});
            skArc(sketch, "E25.trimOffspring", {"start": v(-18.73, 3.48) * mm, "mid": v(-19.05, 0) * mm, "end": v(-18.73, -3.48) * mm});
            skArc(sketch, "E26.trimOffspring", {"start": v(-6.35, 17.96) * mm, "mid": v(-9.52, 16.5) * mm, "end": v(-12.38, 14.48) * mm});
            skArc(sketch, "E27.trimOffspring", {"start": v(12.38, 14.48) * mm, "mid": v(9.53, 16.5) * mm, "end": v(6.35, 17.96) * mm});
            skPoint(sketch, "E28.orphan", {"position": v(6.35, 0) * mm});
            skArc(sketch, "E29.trimOffspring", {"start": v(6.35, -17.96) * mm, "mid": v(9.52, -16.5) * mm, "end": v(12.38, -14.48) * mm});
            skArc(sketch, "E30.trimOffspring", {"start": v(18.73, -3.48) * mm, "mid": v(19.05, 0) * mm, "end": v(18.73, 3.48) * mm});
            skSolve(sketch);
        }
        {
            var Q0;
            Q0=qSketchRegion(id+"F7",true);
            extrude(context, id + "F8", {"entities" : qUnion([Q0]), "operationType" : NewBodyOperationType.REMOVE, "endBound" : BoundingType.THROUGH_ALL, "oppositeDirection" : true, "depth" : 25.4 * mm});
        }
        {
            var Q0;
            Q0=makeQuery(id+"F5.opExtrude","CAP_FACE",FACE,{"disambiguationData":[OSD([sQuery(id+"F4.wireOp",EDGE,"E10")])],"isStart":false});
            var sketch = newSketch(context, id + "F9", { "sketchPlane" : qUnion([Q0])});
            skCircle(sketch, "E31", {"center": v(0, 0) * mm, "radius": 6.35 * mm});
            skSolve(sketch);
        }
        {
            var Q0;
            Q0=qSketchRegion(id+"F9",true);
            extrude(context, id + "F10", {"entities" : qUnion([Q0]), "operationType" : NewBodyOperationType.REMOVE, "endBound" : BoundingType.THROUGH_ALL, "oppositeDirection" : true, "depth" : 25.4 * mm});
        }
        {
            var Q0;
            Q0=makeQuery(id+"F5.opExtrude","SWEPT_BODY",BODY,{"disambiguationData":[OSD([sQuery(id+"F4.wireOp",EDGE,"E10")])]});
            deleteBodies(context, id + "F11", {"entities" : qUnion([Q0])});
        }
        {
            var Q0;
            Q0=qCreatedBy(makeId("Right.planeOp"),FACE);
            var sketch = newSketch(context, id + "F12", { "sketchPlane" : qUnion([Q0])});
            skLineSegment(sketch, "E32", {"start": v(-113.32, 3.36) * mm, "end": v(-113.32, 9.34) * mm});
            skLineSegment(sketch, "E33", {"start": v(-113.32, 9.34) * mm, "end": v(-101.6, 12.7) * mm});
            skLineSegment(sketch, "E34", {"start": v(-101.6, 0) * mm, "end": v(-113.32, 3.36) * mm});
            skLineSegment(sketch, "E35", {"start": v(-101.6, 0) * mm, "end": v(-101.6, 0) * mm});
            skLineSegment(sketch, "E36", {"start": v(-101.6, 0) * mm, "end": v(-119.44, 0) * mm});
            skLineSegment(sketch, "E37", {"start": v(-119.44, 0) * mm, "end": v(-119.44, 12.7) * mm});
            skLineSegment(sketch, "E38", {"start": v(-119.44, 12.7) * mm, "end": v(-101.6, 12.7) * mm});
            skLineSegment(sketch, "E39", {"start": v(0, 0) * mm, "end": v(0, -54.5) * mm, "construction": true});
            skSolve(sketch);
        }
        {
            var Q0;
            Q0=qSketchRegion(id+"F12",true);
            var Q1;
            Q1=sQuery(id+"F12.wireOp",EDGE,"E39");
            revolve(context, id + "F13", {"operationType" : NewBodyOperationType.REMOVE, "entities" : qUnion([Q0]), "axis" : qUnion([Q1]), "revolveType" : RevolveType.FULL, "oppositeDirection" : true});
        }
        {
            var Q0;
            Q0=qCreatedBy(makeId("Top.planeOp"),FACE);
            var sketch = newSketch(context, id + "F14", { "sketchPlane" : qUnion([Q0])});
            skLineSegment(sketch, "E40", {"start": v(0, 0) * mm, "end": v(-15.83, 202.58) * mm, "construction": true});
            skLineSegment(sketch, "E41.bottom", {"start": v(0, 111.12) * mm, "end": v(-8.36, 110.47) * mm, "construction": true});
            skLineSegment(sketch, "E42", {"start": v(0, 0) * mm, "end": v(0, 118.5) * mm, "construction": true});
            skLineSegment(sketch, "E43", {"start": v(0, 111.12) * mm, "end": v(-9.22, 118) * mm});
            skPoint(sketch, "E44.MirrorCS.end.orphan", {"position": v(-9.22, 118) * mm});
            skPoint(sketch, "E45.center", {"position": v(0, 0) * mm});
            skArc(sketch, "E46.MirrorCS", {"start": v(-3.98, 107.75) * mm, "mid": v(-3.69, 107.83) * mm, "end": v(-3.45, 108.02) * mm});
            skLineSegment(sketch, "E47.MirrorCS", {"start": v(-8.54, 107.4) * mm, "end": v(-3.98, 107.75) * mm});
            skArc(sketch, "E48", {"start": v(0, 111.12) * mm, "mid": v(-1.46, 110.62) * mm, "end": v(-2.3, 109.33) * mm});
            skLineSegment(sketch, "E49", {"start": v(-2.3, 109.33) * mm, "end": v(-2.3, 109.33) * mm});
            skPoint(sketch, "E50.trimOffspring.end.orphan", {"position": v(-1.5, 110.55) * mm});
            skLineSegment(sketch, "E51.MirrorCS", {"start": v(-14.7, 108.36) * mm, "end": v(-14.73, 108.36) * mm});
            skPoint(sketch, "E52.center", {"position": v(0.06, -0.13) * mm});
            skLineSegment(sketch, "E53", {"start": v(-2.3, 109.33) * mm, "end": v(-2.73, 109.33) * mm});
            skLineSegment(sketch, "E54", {"start": v(-2.73, 109.33) * mm, "end": v(-3.45, 108.02) * mm});
            skArc(sketch, "E55.MirrorCS", {"start": v(-17.27, 109.77) * mm, "mid": v(-15.75, 109.5) * mm, "end": v(-14.7, 108.36) * mm});
            skLineSegment(sketch, "E56.MirrorCS", {"start": v(-14.73, 108.36) * mm, "end": v(-14.3, 108.43) * mm});
            skArc(sketch, "E57.MirrorCS", {"start": v(-12.81, 107.06) * mm, "mid": v(-13.11, 107.1) * mm, "end": v(-13.38, 107.24) * mm});
            skLineSegment(sketch, "E58.MirrorCS", {"start": v(-14.3, 108.43) * mm, "end": v(-13.38, 107.24) * mm});
            skLineSegment(sketch, "E59.MirrorCS", {"start": v(-17.27, 109.77) * mm, "end": v(-9.22, 118) * mm});
            skLineSegment(sketch, "E60.MirrorCS", {"start": v(-8.25, 107.42) * mm, "end": v(-12.81, 107.06) * mm});
            skLineSegment(sketch, "E61.1.0", {"start": v(-34.23, 105.72) * mm, "end": v(-27.57, 115.11) * mm});
            skLineSegment(sketch, "E61.1.1", {"start": v(-17.38, 109.75) * mm, "end": v(-27.57, 115.11) * mm});
            skLineSegment(sketch, "E61.1.2", {"start": v(-24.95, 104.8) * mm, "end": v(-29.4, 103.74) * mm});
            skLineSegment(sketch, "E61.1.3", {"start": v(-31.08, 104.86) * mm, "end": v(-30, 103.83) * mm});
            skArc(sketch, "E61.1.4", {"start": v(-29.4, 103.74) * mm, "mid": v(-29.7, 103.73) * mm, "end": v(-30, 103.83) * mm});
            skLineSegment(sketch, "E61.1.5", {"start": v(-31.5, 104.72) * mm, "end": v(-31.08, 104.86) * mm});
            skArc(sketch, "E61.1.6", {"start": v(-34.23, 105.72) * mm, "mid": v(-32.68, 105.7) * mm, "end": v(-31.48, 104.73) * mm});
            skLineSegment(sketch, "E61.1.7", {"start": v(-31.48, 104.73) * mm, "end": v(-31.5, 104.72) * mm});
            skLineSegment(sketch, "E61.1.8", {"start": v(-31.48, 104.73) * mm, "end": v(-31.5, 104.72) * mm});
            skArc(sketch, "E61.1.9", {"start": v(-20.79, 105.8) * mm, "mid": v(-20.5, 105.93) * mm, "end": v(-20.3, 106.15) * mm});
            skLineSegment(sketch, "E61.1.10", {"start": v(-25.24, 104.74) * mm, "end": v(-20.79, 105.8) * mm});
            skLineSegment(sketch, "E61.1.11", {"start": v(-19.8, 107.56) * mm, "end": v(-20.3, 106.15) * mm});
            skArc(sketch, "E61.1.12", {"start": v(-17.38, 109.75) * mm, "mid": v(-18.75, 109.03) * mm, "end": v(-19.38, 107.63) * mm});
            skLineSegment(sketch, "E61.1.13", {"start": v(-19.37, 107.63) * mm, "end": v(-19.8, 107.56) * mm});
            skLineSegment(sketch, "E61.2.0", {"start": v(-50.34, 99.07) * mm, "end": v(-45.24, 109.38) * mm});
            skLineSegment(sketch, "E61.2.1", {"start": v(-34.34, 105.68) * mm, "end": v(-45.24, 109.38) * mm});
            skLineSegment(sketch, "E61.2.2", {"start": v(-41.04, 99.61) * mm, "end": v(-45.27, 97.86) * mm});
            skLineSegment(sketch, "E61.2.3", {"start": v(-47.1, 98.7) * mm, "end": v(-45.87, 97.86) * mm});
            skArc(sketch, "E61.2.4", {"start": v(-45.27, 97.86) * mm, "mid": v(-45.57, 97.8) * mm, "end": v(-45.87, 97.86) * mm});
            skLineSegment(sketch, "E61.2.5", {"start": v(-47.5, 98.5) * mm, "end": v(-47.1, 98.7) * mm});
            skArc(sketch, "E61.2.6", {"start": v(-50.34, 99.07) * mm, "mid": v(-48.81, 99.28) * mm, "end": v(-47.48, 98.51) * mm});
            skLineSegment(sketch, "E61.2.7", {"start": v(-47.48, 98.51) * mm, "end": v(-47.5, 98.5) * mm});
            skLineSegment(sketch, "E61.2.8", {"start": v(-47.48, 98.51) * mm, "end": v(-47.5, 98.5) * mm});
            skArc(sketch, "E61.2.9", {"start": v(-37.08, 101.25) * mm, "mid": v(-36.83, 101.42) * mm, "end": v(-36.66, 101.67) * mm});
            skLineSegment(sketch, "E61.2.10", {"start": v(-41.31, 99.5) * mm, "end": v(-37.08, 101.25) * mm});
            skLineSegment(sketch, "E61.2.11", {"start": v(-36.38, 103.14) * mm, "end": v(-36.66, 101.67) * mm});
            skArc(sketch, "E61.2.12", {"start": v(-34.34, 105.68) * mm, "mid": v(-35.57, 104.76) * mm, "end": v(-35.98, 103.27) * mm});
            skLineSegment(sketch, "E61.2.13", {"start": v(-35.96, 103.27) * mm, "end": v(-36.38, 103.14) * mm});
            skLineSegment(sketch, "E61.3.0", {"start": v(-65.22, 89.97) * mm, "end": v(-61.8, 100.96) * mm});
            skLineSegment(sketch, "E61.3.1", {"start": v(-50.45, 99.01) * mm, "end": v(-61.8, 100.96) * mm});
            skLineSegment(sketch, "E61.3.2", {"start": v(-56.12, 91.97) * mm, "end": v(-60.02, 89.58) * mm});
            skLineSegment(sketch, "E61.3.3", {"start": v(-61.96, 90.12) * mm, "end": v(-60.6, 89.48) * mm});
            skArc(sketch, "E61.3.4", {"start": v(-60.02, 89.58) * mm, "mid": v(-60.3, 89.47) * mm, "end": v(-60.6, 89.48) * mm});
            skLineSegment(sketch, "E61.3.5", {"start": v(-62.32, 89.86) * mm, "end": v(-61.96, 90.12) * mm});
            skArc(sketch, "E61.3.6", {"start": v(-65.22, 89.97) * mm, "mid": v(-63.74, 90.42) * mm, "end": v(-62.3, 89.87) * mm});
            skLineSegment(sketch, "E61.3.7", {"start": v(-62.3, 89.87) * mm, "end": v(-62.32, 89.86) * mm});
            skLineSegment(sketch, "E61.3.8", {"start": v(-62.3, 89.87) * mm, "end": v(-62.32, 89.86) * mm});
            skArc(sketch, "E61.3.9", {"start": v(-52.46, 94.2) * mm, "mid": v(-52.24, 94.4) * mm, "end": v(-52.1, 94.68) * mm});
            skLineSegment(sketch, "E61.3.10", {"start": v(-56.37, 91.81) * mm, "end": v(-52.46, 94.2) * mm});
            skLineSegment(sketch, "E61.3.11", {"start": v(-52.07, 96.18) * mm, "end": v(-52.1, 94.68) * mm});
            skArc(sketch, "E61.3.12", {"start": v(-50.45, 99.01) * mm, "mid": v(-51.52, 97.9) * mm, "end": v(-51.7, 96.37) * mm});
            skLineSegment(sketch, "E61.3.13", {"start": v(-51.68, 96.38) * mm, "end": v(-52.07, 96.18) * mm});
            skLineSegment(sketch, "E61.4.0", {"start": v(-78.5, 78.66) * mm, "end": v(-76.83, 90.05) * mm});
            skLineSegment(sketch, "E61.4.1", {"start": v(-65.32, 89.9) * mm, "end": v(-76.83, 90.05) * mm});
            skLineSegment(sketch, "E61.4.2", {"start": v(-69.81, 82.06) * mm, "end": v(-73.3, 79.08) * mm});
            skLineSegment(sketch, "E61.4.3", {"start": v(-75.3, 79.32) * mm, "end": v(-73.86, 78.9) * mm});
            skArc(sketch, "E61.4.4", {"start": v(-73.3, 79.08) * mm, "mid": v(-73.56, 78.94) * mm, "end": v(-73.86, 78.9) * mm});
            skLineSegment(sketch, "E61.4.5", {"start": v(-75.6, 79) * mm, "end": v(-75.3, 79.32) * mm});
            skArc(sketch, "E61.4.6", {"start": v(-78.5, 78.66) * mm, "mid": v(-77.1, 79.34) * mm, "end": v(-75.6, 79.02) * mm});
            skLineSegment(sketch, "E61.4.7", {"start": v(-75.6, 79.02) * mm, "end": v(-75.6, 79) * mm});
            skLineSegment(sketch, "E61.4.8", {"start": v(-75.6, 79.02) * mm, "end": v(-75.6, 79) * mm});
            skArc(sketch, "E61.4.9", {"start": v(-66.55, 84.83) * mm, "mid": v(-66.37, 85.07) * mm, "end": v(-66.28, 85.36) * mm});
            skLineSegment(sketch, "E61.4.10", {"start": v(-70.04, 81.86) * mm, "end": v(-66.55, 84.83) * mm});
            skLineSegment(sketch, "E61.4.11", {"start": v(-66.47, 86.85) * mm, "end": v(-66.28, 85.36) * mm});
            skArc(sketch, "E61.4.12", {"start": v(-65.32, 89.9) * mm, "mid": v(-66.2, 88.64) * mm, "end": v(-66.13, 87.1) * mm});
            skLineSegment(sketch, "E61.4.13", {"start": v(-66.12, 87.1) * mm, "end": v(-66.47, 86.85) * mm});
            skLineSegment(sketch, "E61.5.0", {"start": v(-89.83, 65.41) * mm, "end": v(-89.97, 76.92) * mm});
            skLineSegment(sketch, "E61.5.1", {"start": v(-78.58, 78.58) * mm, "end": v(-89.97, 76.92) * mm});
            skLineSegment(sketch, "E61.5.2", {"start": v(-81.79, 70.13) * mm, "end": v(-84.76, 66.65) * mm});
            skLineSegment(sketch, "E61.5.3", {"start": v(-86.78, 66.56) * mm, "end": v(-85.3, 66.37) * mm});
            skArc(sketch, "E61.5.4", {"start": v(-84.76, 66.65) * mm, "mid": v(-85, 66.46) * mm, "end": v(-85.3, 66.37) * mm});
            skLineSegment(sketch, "E61.5.5", {"start": v(-87.03, 66.2) * mm, "end": v(-86.78, 66.56) * mm});
            skArc(sketch, "E61.5.6", {"start": v(-89.83, 65.41) * mm, "mid": v(-88.57, 66.3) * mm, "end": v(-87.03, 66.22) * mm});
            skLineSegment(sketch, "E61.5.7", {"start": v(-87.03, 66.22) * mm, "end": v(-87.03, 66.2) * mm});
            skLineSegment(sketch, "E61.5.8", {"start": v(-87.03, 66.22) * mm, "end": v(-87.03, 66.2) * mm});
            skArc(sketch, "E61.5.9", {"start": v(-79, 73.38) * mm, "mid": v(-78.86, 73.64) * mm, "end": v(-78.82, 73.95) * mm});
            skLineSegment(sketch, "E61.5.10", {"start": v(-81.98, 69.9) * mm, "end": v(-79, 73.38) * mm});
            skLineSegment(sketch, "E61.5.11", {"start": v(-79.24, 75.38) * mm, "end": v(-78.82, 73.95) * mm});
            skArc(sketch, "E61.5.12", {"start": v(-78.58, 78.58) * mm, "mid": v(-79.25, 77.19) * mm, "end": v(-78.94, 75.68) * mm});
            skLineSegment(sketch, "E61.5.13", {"start": v(-78.93, 75.7) * mm, "end": v(-79.24, 75.38) * mm});
            skLineSegment(sketch, "E61.6.0", {"start": v(-98.96, 50.55) * mm, "end": v(-100.9, 61.9) * mm});
            skLineSegment(sketch, "E61.6.1", {"start": v(-89.9, 65.32) * mm, "end": v(-100.9, 61.9) * mm});
            skLineSegment(sketch, "E61.6.2", {"start": v(-91.75, 56.47) * mm, "end": v(-94.15, 52.56) * mm});
            skLineSegment(sketch, "E61.6.3", {"start": v(-96.12, 52.17) * mm, "end": v(-94.63, 52.21) * mm});
            skArc(sketch, "E61.6.4", {"start": v(-94.15, 52.56) * mm, "mid": v(-94.35, 52.34) * mm, "end": v(-94.63, 52.21) * mm});
            skLineSegment(sketch, "E61.6.5", {"start": v(-96.32, 51.78) * mm, "end": v(-96.12, 52.17) * mm});
            skArc(sketch, "E61.6.6", {"start": v(-98.96, 50.55) * mm, "mid": v(-97.85, 51.63) * mm, "end": v(-96.31, 51.8) * mm});
            skLineSegment(sketch, "E61.6.7", {"start": v(-96.31, 51.8) * mm, "end": v(-96.32, 51.78) * mm});
            skLineSegment(sketch, "E61.6.8", {"start": v(-96.31, 51.8) * mm, "end": v(-96.32, 51.78) * mm});
            skArc(sketch, "E61.6.9", {"start": v(-89.51, 60.12) * mm, "mid": v(-89.4, 60.4) * mm, "end": v(-89.41, 60.7) * mm});
            skLineSegment(sketch, "E61.6.10", {"start": v(-91.9, 56.21) * mm, "end": v(-89.51, 60.12) * mm});
            skLineSegment(sketch, "E61.6.11", {"start": v(-90.06, 62.06) * mm, "end": v(-89.41, 60.7) * mm});
            skArc(sketch, "E61.6.12", {"start": v(-89.9, 65.32) * mm, "mid": v(-90.35, 63.84) * mm, "end": v(-89.8, 62.4) * mm});
            skLineSegment(sketch, "E61.6.13", {"start": v(-89.8, 62.41) * mm, "end": v(-90.06, 62.06) * mm});
            skLineSegment(sketch, "E61.7.0", {"start": v(-105.65, 34.45) * mm, "end": v(-109.33, 45.36) * mm});
            skLineSegment(sketch, "E61.7.1", {"start": v(-99.01, 50.45) * mm, "end": v(-109.33, 45.36) * mm});
            skLineSegment(sketch, "E61.7.2", {"start": v(-99.46, 41.42) * mm, "end": v(-101.2, 37.2) * mm});
            skLineSegment(sketch, "E61.7.3", {"start": v(-103.1, 36.5) * mm, "end": v(-101.63, 36.77) * mm});
            skArc(sketch, "E61.7.4", {"start": v(-101.2, 37.2) * mm, "mid": v(-101.38, 36.94) * mm, "end": v(-101.63, 36.77) * mm});
            skLineSegment(sketch, "E61.7.5", {"start": v(-103.24, 36.07) * mm, "end": v(-103.1, 36.5) * mm});
            skArc(sketch, "E61.7.6", {"start": v(-105.65, 34.45) * mm, "mid": v(-104.72, 35.68) * mm, "end": v(-103.23, 36.09) * mm});
            skLineSegment(sketch, "E61.7.7", {"start": v(-103.23, 36.09) * mm, "end": v(-103.24, 36.07) * mm});
            skLineSegment(sketch, "E61.7.8", {"start": v(-103.23, 36.09) * mm, "end": v(-103.24, 36.07) * mm});
            skArc(sketch, "E61.7.9", {"start": v(-97.82, 45.37) * mm, "mid": v(-97.75, 45.67) * mm, "end": v(-97.81, 45.97) * mm});
            skLineSegment(sketch, "E61.7.10", {"start": v(-99.57, 41.14) * mm, "end": v(-97.82, 45.37) * mm});
            skLineSegment(sketch, "E61.7.11", {"start": v(-98.65, 47.2) * mm, "end": v(-97.81, 45.97) * mm});
            skArc(sketch, "E61.7.12", {"start": v(-99.01, 50.45) * mm, "mid": v(-99.23, 48.92) * mm, "end": v(-98.46, 47.58) * mm});
            skLineSegment(sketch, "E61.7.13", {"start": v(-98.46, 47.6) * mm, "end": v(-98.65, 47.2) * mm});
            skLineSegment(sketch, "E61.8.0", {"start": v(-109.74, 17.5) * mm, "end": v(-115.08, 27.7) * mm});
            skLineSegment(sketch, "E61.8.1", {"start": v(-105.68, 34.34) * mm, "end": v(-115.08, 27.7) * mm});
            skLineSegment(sketch, "E61.8.2", {"start": v(-104.71, 25.35) * mm, "end": v(-105.78, 20.9) * mm});
            skLineSegment(sketch, "E61.8.3", {"start": v(-107.54, 19.91) * mm, "end": v(-106.13, 20.41) * mm});
            skArc(sketch, "E61.8.4", {"start": v(-105.78, 20.9) * mm, "mid": v(-105.9, 20.62) * mm, "end": v(-106.13, 20.41) * mm});
            skLineSegment(sketch, "E61.8.5", {"start": v(-107.6, 19.48) * mm, "end": v(-107.54, 19.91) * mm});
            skArc(sketch, "E61.8.6", {"start": v(-109.74, 17.5) * mm, "mid": v(-109.01, 18.86) * mm, "end": v(-107.6, 19.5) * mm});
            skLineSegment(sketch, "E61.8.7", {"start": v(-107.6, 19.5) * mm, "end": v(-107.6, 19.48) * mm});
            skLineSegment(sketch, "E61.8.8", {"start": v(-107.6, 19.5) * mm, "end": v(-107.6, 19.48) * mm});
            skArc(sketch, "E61.8.9", {"start": v(-103.7, 29.51) * mm, "mid": v(-103.7, 29.82) * mm, "end": v(-103.8, 30.1) * mm});
            skLineSegment(sketch, "E61.8.10", {"start": v(-104.78, 25.06) * mm, "end": v(-103.7, 29.51) * mm});
            skLineSegment(sketch, "E61.8.11", {"start": v(-104.82, 31.2) * mm, "end": v(-103.8, 30.1) * mm});
            skArc(sketch, "E61.8.12", {"start": v(-105.68, 34.34) * mm, "mid": v(-105.66, 32.8) * mm, "end": v(-104.7, 31.6) * mm});
            skLineSegment(sketch, "E61.8.13", {"start": v(-104.69, 31.6) * mm, "end": v(-104.82, 31.2) * mm});
            skLineSegment(sketch, "E61.9.0", {"start": v(-111.12, 0.12) * mm, "end": v(-118, 9.35) * mm});
            skLineSegment(sketch, "E61.9.1", {"start": v(-109.75, 17.38) * mm, "end": v(-118, 9.35) * mm});
            skLineSegment(sketch, "E61.9.2", {"start": v(-107.39, 8.66) * mm, "end": v(-107.75, 4.1) * mm});
            skLineSegment(sketch, "E61.9.3", {"start": v(-109.33, 2.85) * mm, "end": v(-108.02, 3.56) * mm});
            skArc(sketch, "E61.9.4", {"start": v(-107.75, 4.1) * mm, "mid": v(-107.83, 3.8) * mm, "end": v(-108.02, 3.56) * mm});
            skLineSegment(sketch, "E61.9.5", {"start": v(-109.33, 2.4) * mm, "end": v(-109.33, 2.85) * mm});
            skArc(sketch, "E61.9.6", {"start": v(-111.12, 0.12) * mm, "mid": v(-110.62, 1.58) * mm, "end": v(-109.33, 2.42) * mm});
            skLineSegment(sketch, "E61.9.7", {"start": v(-109.33, 2.42) * mm, "end": v(-109.33, 2.4) * mm});
            skLineSegment(sketch, "E61.9.8", {"start": v(-109.33, 2.42) * mm, "end": v(-109.33, 2.4) * mm});
            skArc(sketch, "E61.9.9", {"start": v(-107.05, 12.93) * mm, "mid": v(-107.08, 13.23) * mm, "end": v(-107.23, 13.5) * mm});
            skLineSegment(sketch, "E61.9.10", {"start": v(-107.41, 8.36) * mm, "end": v(-107.05, 12.93) * mm});
            skLineSegment(sketch, "E61.9.11", {"start": v(-108.41, 14.4) * mm, "end": v(-107.23, 13.5) * mm});
            skArc(sketch, "E61.9.12", {"start": v(-109.75, 17.38) * mm, "mid": v(-109.49, 15.86) * mm, "end": v(-108.35, 14.82) * mm});
            skLineSegment(sketch, "E61.9.13", {"start": v(-108.34, 14.84) * mm, "end": v(-108.41, 14.4) * mm});
            skLineSegment(sketch, "E61.10.0", {"start": v(-109.77, -17.27) * mm, "end": v(-118, -9.22) * mm});
            skLineSegment(sketch, "E61.10.1", {"start": v(-111.12, 0) * mm, "end": v(-118, -9.22) * mm});
            skLineSegment(sketch, "E61.10.2", {"start": v(-107.42, -8.25) * mm, "end": v(-107.06, -12.81) * mm});
            skLineSegment(sketch, "E61.10.3", {"start": v(-108.43, -14.3) * mm, "end": v(-107.24, -13.38) * mm});
            skArc(sketch, "E61.10.4", {"start": v(-107.06, -12.81) * mm, "mid": v(-107.1, -13.11) * mm, "end": v(-107.24, -13.38) * mm});
            skLineSegment(sketch, "E61.10.5", {"start": v(-108.36, -14.73) * mm, "end": v(-108.43, -14.3) * mm});
            skArc(sketch, "E61.10.6", {"start": v(-109.77, -17.27) * mm, "mid": v(-109.5, -15.75) * mm, "end": v(-108.36, -14.7) * mm});
            skLineSegment(sketch, "E61.10.7", {"start": v(-108.36, -14.7) * mm, "end": v(-108.36, -14.73) * mm});
            skLineSegment(sketch, "E61.10.8", {"start": v(-108.36, -14.7) * mm, "end": v(-108.36, -14.73) * mm});
            skArc(sketch, "E61.10.9", {"start": v(-107.75, -3.98) * mm, "mid": v(-107.83, -3.69) * mm, "end": v(-108.02, -3.45) * mm});
            skLineSegment(sketch, "E61.10.10", {"start": v(-107.4, -8.54) * mm, "end": v(-107.75, -3.98) * mm});
            skLineSegment(sketch, "E61.10.11", {"start": v(-109.33, -2.73) * mm, "end": v(-108.02, -3.45) * mm});
            skArc(sketch, "E61.10.12", {"start": v(-111.12, 0) * mm, "mid": v(-110.62, -1.46) * mm, "end": v(-109.33, -2.3) * mm});
            skLineSegment(sketch, "E61.10.13", {"start": v(-109.33, -2.3) * mm, "end": v(-109.33, -2.73) * mm});
            skLineSegment(sketch, "E61.11.0", {"start": v(-105.72, -34.23) * mm, "end": v(-115.11, -27.57) * mm});
            skLineSegment(sketch, "E61.11.1", {"start": v(-109.75, -17.38) * mm, "end": v(-115.11, -27.57) * mm});
            skLineSegment(sketch, "E61.11.2", {"start": v(-104.8, -24.95) * mm, "end": v(-103.74, -29.4) * mm});
            skLineSegment(sketch, "E61.11.3", {"start": v(-104.86, -31.08) * mm, "end": v(-103.83, -30) * mm});
            skArc(sketch, "E61.11.4", {"start": v(-103.74, -29.4) * mm, "mid": v(-103.73, -29.7) * mm, "end": v(-103.83, -30) * mm});
            skLineSegment(sketch, "E61.11.5", {"start": v(-104.72, -31.5) * mm, "end": v(-104.86, -31.08) * mm});
            skArc(sketch, "E61.11.6", {"start": v(-105.72, -34.23) * mm, "mid": v(-105.7, -32.68) * mm, "end": v(-104.73, -31.48) * mm});
            skLineSegment(sketch, "E61.11.7", {"start": v(-104.73, -31.48) * mm, "end": v(-104.72, -31.5) * mm});
            skLineSegment(sketch, "E61.11.8", {"start": v(-104.73, -31.48) * mm, "end": v(-104.72, -31.5) * mm});
            skArc(sketch, "E61.11.9", {"start": v(-105.8, -20.79) * mm, "mid": v(-105.93, -20.5) * mm, "end": v(-106.15, -20.3) * mm});
            skLineSegment(sketch, "E61.11.10", {"start": v(-104.74, -25.24) * mm, "end": v(-105.8, -20.79) * mm});
            skLineSegment(sketch, "E61.11.11", {"start": v(-107.56, -19.8) * mm, "end": v(-106.15, -20.3) * mm});
            skArc(sketch, "E61.11.12", {"start": v(-109.75, -17.38) * mm, "mid": v(-109.03, -18.75) * mm, "end": v(-107.63, -19.38) * mm});
            skLineSegment(sketch, "E61.11.13", {"start": v(-107.63, -19.37) * mm, "end": v(-107.56, -19.8) * mm});
            skLineSegment(sketch, "E61.12.0", {"start": v(-99.07, -50.34) * mm, "end": v(-109.38, -45.24) * mm});
            skLineSegment(sketch, "E61.12.1", {"start": v(-105.68, -34.34) * mm, "end": v(-109.38, -45.24) * mm});
            skLineSegment(sketch, "E61.12.2", {"start": v(-99.61, -41.04) * mm, "end": v(-97.86, -45.27) * mm});
            skLineSegment(sketch, "E61.12.3", {"start": v(-98.7, -47.1) * mm, "end": v(-97.86, -45.87) * mm});
            skArc(sketch, "E61.12.4", {"start": v(-97.86, -45.27) * mm, "mid": v(-97.8, -45.57) * mm, "end": v(-97.86, -45.87) * mm});
            skLineSegment(sketch, "E61.12.5", {"start": v(-98.5, -47.5) * mm, "end": v(-98.7, -47.1) * mm});
            skArc(sketch, "E61.12.6", {"start": v(-99.07, -50.34) * mm, "mid": v(-99.28, -48.81) * mm, "end": v(-98.51, -47.48) * mm});
            skLineSegment(sketch, "E61.12.7", {"start": v(-98.51, -47.48) * mm, "end": v(-98.5, -47.5) * mm});
            skLineSegment(sketch, "E61.12.8", {"start": v(-98.51, -47.48) * mm, "end": v(-98.5, -47.5) * mm});
            skArc(sketch, "E61.12.9", {"start": v(-101.25, -37.08) * mm, "mid": v(-101.42, -36.83) * mm, "end": v(-101.67, -36.66) * mm});
            skLineSegment(sketch, "E61.12.10", {"start": v(-99.5, -41.31) * mm, "end": v(-101.25, -37.08) * mm});
            skLineSegment(sketch, "E61.12.11", {"start": v(-103.14, -36.38) * mm, "end": v(-101.67, -36.66) * mm});
            skArc(sketch, "E61.12.12", {"start": v(-105.68, -34.34) * mm, "mid": v(-104.76, -35.57) * mm, "end": v(-103.27, -35.98) * mm});
            skLineSegment(sketch, "E61.12.13", {"start": v(-103.27, -35.96) * mm, "end": v(-103.14, -36.38) * mm});
            skLineSegment(sketch, "E61.13.0", {"start": v(-89.97, -65.22) * mm, "end": v(-100.96, -61.8) * mm});
            skLineSegment(sketch, "E61.13.1", {"start": v(-99.01, -50.45) * mm, "end": v(-100.96, -61.8) * mm});
            skLineSegment(sketch, "E61.13.2", {"start": v(-91.97, -56.12) * mm, "end": v(-89.58, -60.02) * mm});
            skLineSegment(sketch, "E61.13.3", {"start": v(-90.12, -61.96) * mm, "end": v(-89.48, -60.6) * mm});
            skArc(sketch, "E61.13.4", {"start": v(-89.58, -60.02) * mm, "mid": v(-89.47, -60.3) * mm, "end": v(-89.48, -60.6) * mm});
            skLineSegment(sketch, "E61.13.5", {"start": v(-89.86, -62.32) * mm, "end": v(-90.12, -61.96) * mm});
            skArc(sketch, "E61.13.6", {"start": v(-89.97, -65.22) * mm, "mid": v(-90.42, -63.74) * mm, "end": v(-89.87, -62.3) * mm});
            skLineSegment(sketch, "E61.13.7", {"start": v(-89.87, -62.3) * mm, "end": v(-89.86, -62.32) * mm});
            skLineSegment(sketch, "E61.13.8", {"start": v(-89.87, -62.3) * mm, "end": v(-89.86, -62.32) * mm});
            skArc(sketch, "E61.13.9", {"start": v(-94.2, -52.46) * mm, "mid": v(-94.4, -52.24) * mm, "end": v(-94.68, -52.1) * mm});
            skLineSegment(sketch, "E61.13.10", {"start": v(-91.81, -56.37) * mm, "end": v(-94.2, -52.46) * mm});
            skLineSegment(sketch, "E61.13.11", {"start": v(-96.18, -52.07) * mm, "end": v(-94.68, -52.1) * mm});
            skArc(sketch, "E61.13.12", {"start": v(-99.01, -50.45) * mm, "mid": v(-97.9, -51.52) * mm, "end": v(-96.37, -51.7) * mm});
            skLineSegment(sketch, "E61.13.13", {"start": v(-96.38, -51.68) * mm, "end": v(-96.18, -52.07) * mm});
            skLineSegment(sketch, "E61.14.0", {"start": v(-78.66, -78.5) * mm, "end": v(-90.05, -76.83) * mm});
            skLineSegment(sketch, "E61.14.1", {"start": v(-89.9, -65.32) * mm, "end": v(-90.05, -76.83) * mm});
            skLineSegment(sketch, "E61.14.2", {"start": v(-82.06, -69.81) * mm, "end": v(-79.08, -73.3) * mm});
            skLineSegment(sketch, "E61.14.3", {"start": v(-79.32, -75.3) * mm, "end": v(-78.9, -73.86) * mm});
            skArc(sketch, "E61.14.4", {"start": v(-79.08, -73.3) * mm, "mid": v(-78.94, -73.56) * mm, "end": v(-78.9, -73.86) * mm});
            skLineSegment(sketch, "E61.14.5", {"start": v(-79, -75.6) * mm, "end": v(-79.32, -75.3) * mm});
            skArc(sketch, "E61.14.6", {"start": v(-78.66, -78.5) * mm, "mid": v(-79.34, -77.1) * mm, "end": v(-79.02, -75.6) * mm});
            skLineSegment(sketch, "E61.14.7", {"start": v(-79.02, -75.6) * mm, "end": v(-79, -75.6) * mm});
            skLineSegment(sketch, "E61.14.8", {"start": v(-79.02, -75.6) * mm, "end": v(-79, -75.6) * mm});
            skArc(sketch, "E61.14.9", {"start": v(-84.83, -66.55) * mm, "mid": v(-85.07, -66.37) * mm, "end": v(-85.36, -66.28) * mm});
            skLineSegment(sketch, "E61.14.10", {"start": v(-81.86, -70.04) * mm, "end": v(-84.83, -66.55) * mm});
            skLineSegment(sketch, "E61.14.11", {"start": v(-86.85, -66.47) * mm, "end": v(-85.36, -66.28) * mm});
            skArc(sketch, "E61.14.12", {"start": v(-89.9, -65.32) * mm, "mid": v(-88.64, -66.2) * mm, "end": v(-87.1, -66.13) * mm});
            skLineSegment(sketch, "E61.14.13", {"start": v(-87.1, -66.12) * mm, "end": v(-86.85, -66.47) * mm});
            skLineSegment(sketch, "E61.15.0", {"start": v(-65.41, -89.83) * mm, "end": v(-76.92, -89.97) * mm});
            skLineSegment(sketch, "E61.15.1", {"start": v(-78.58, -78.58) * mm, "end": v(-76.92, -89.97) * mm});
            skLineSegment(sketch, "E61.15.2", {"start": v(-70.13, -81.79) * mm, "end": v(-66.65, -84.76) * mm});
            skLineSegment(sketch, "E61.15.3", {"start": v(-66.56, -86.78) * mm, "end": v(-66.37, -85.3) * mm});
            skArc(sketch, "E61.15.4", {"start": v(-66.65, -84.76) * mm, "mid": v(-66.46, -85) * mm, "end": v(-66.37, -85.3) * mm});
            skLineSegment(sketch, "E61.15.5", {"start": v(-66.2, -87.03) * mm, "end": v(-66.56, -86.78) * mm});
            skArc(sketch, "E61.15.6", {"start": v(-65.41, -89.83) * mm, "mid": v(-66.3, -88.57) * mm, "end": v(-66.22, -87.03) * mm});
            skLineSegment(sketch, "E61.15.7", {"start": v(-66.22, -87.03) * mm, "end": v(-66.2, -87.03) * mm});
            skLineSegment(sketch, "E61.15.8", {"start": v(-66.22, -87.03) * mm, "end": v(-66.2, -87.03) * mm});
            skArc(sketch, "E61.15.9", {"start": v(-73.38, -79) * mm, "mid": v(-73.64, -78.86) * mm, "end": v(-73.95, -78.82) * mm});
            skLineSegment(sketch, "E61.15.10", {"start": v(-69.9, -81.98) * mm, "end": v(-73.38, -79) * mm});
            skLineSegment(sketch, "E61.15.11", {"start": v(-75.38, -79.24) * mm, "end": v(-73.95, -78.82) * mm});
            skArc(sketch, "E61.15.12", {"start": v(-78.58, -78.58) * mm, "mid": v(-77.19, -79.25) * mm, "end": v(-75.68, -78.94) * mm});
            skLineSegment(sketch, "E61.15.13", {"start": v(-75.7, -78.93) * mm, "end": v(-75.38, -79.24) * mm});
            skLineSegment(sketch, "E61.16.0", {"start": v(-50.55, -98.96) * mm, "end": v(-61.9, -100.9) * mm});
            skLineSegment(sketch, "E61.16.1", {"start": v(-65.32, -89.9) * mm, "end": v(-61.9, -100.9) * mm});
            skLineSegment(sketch, "E61.16.2", {"start": v(-56.47, -91.75) * mm, "end": v(-52.56, -94.15) * mm});
            skLineSegment(sketch, "E61.16.3", {"start": v(-52.17, -96.12) * mm, "end": v(-52.21, -94.63) * mm});
            skArc(sketch, "E61.16.4", {"start": v(-52.56, -94.15) * mm, "mid": v(-52.34, -94.35) * mm, "end": v(-52.21, -94.63) * mm});
            skLineSegment(sketch, "E61.16.5", {"start": v(-51.78, -96.32) * mm, "end": v(-52.17, -96.12) * mm});
            skArc(sketch, "E61.16.6", {"start": v(-50.55, -98.96) * mm, "mid": v(-51.63, -97.85) * mm, "end": v(-51.8, -96.31) * mm});
            skLineSegment(sketch, "E61.16.7", {"start": v(-51.8, -96.31) * mm, "end": v(-51.78, -96.32) * mm});
            skLineSegment(sketch, "E61.16.8", {"start": v(-51.8, -96.31) * mm, "end": v(-51.78, -96.32) * mm});
            skArc(sketch, "E61.16.9", {"start": v(-60.12, -89.51) * mm, "mid": v(-60.4, -89.4) * mm, "end": v(-60.7, -89.41) * mm});
            skLineSegment(sketch, "E61.16.10", {"start": v(-56.21, -91.9) * mm, "end": v(-60.12, -89.51) * mm});
            skLineSegment(sketch, "E61.16.11", {"start": v(-62.06, -90.06) * mm, "end": v(-60.7, -89.41) * mm});
            skArc(sketch, "E61.16.12", {"start": v(-65.32, -89.9) * mm, "mid": v(-63.84, -90.35) * mm, "end": v(-62.4, -89.8) * mm});
            skLineSegment(sketch, "E61.16.13", {"start": v(-62.41, -89.8) * mm, "end": v(-62.06, -90.06) * mm});
            skLineSegment(sketch, "E61.17.0", {"start": v(-34.45, -105.65) * mm, "end": v(-45.36, -109.33) * mm});
            skLineSegment(sketch, "E61.17.1", {"start": v(-50.45, -99.01) * mm, "end": v(-45.36, -109.33) * mm});
            skLineSegment(sketch, "E61.17.2", {"start": v(-41.42, -99.46) * mm, "end": v(-37.2, -101.2) * mm});
            skLineSegment(sketch, "E61.17.3", {"start": v(-36.5, -103.1) * mm, "end": v(-36.77, -101.63) * mm});
            skArc(sketch, "E61.17.4", {"start": v(-37.2, -101.2) * mm, "mid": v(-36.94, -101.38) * mm, "end": v(-36.77, -101.63) * mm});
            skLineSegment(sketch, "E61.17.5", {"start": v(-36.07, -103.24) * mm, "end": v(-36.5, -103.1) * mm});
            skArc(sketch, "E61.17.6", {"start": v(-34.45, -105.65) * mm, "mid": v(-35.68, -104.72) * mm, "end": v(-36.09, -103.23) * mm});
            skLineSegment(sketch, "E61.17.7", {"start": v(-36.09, -103.23) * mm, "end": v(-36.07, -103.24) * mm});
            skLineSegment(sketch, "E61.17.8", {"start": v(-36.09, -103.23) * mm, "end": v(-36.07, -103.24) * mm});
            skArc(sketch, "E61.17.9", {"start": v(-45.37, -97.82) * mm, "mid": v(-45.67, -97.75) * mm, "end": v(-45.97, -97.81) * mm});
            skLineSegment(sketch, "E61.17.10", {"start": v(-41.14, -99.57) * mm, "end": v(-45.37, -97.82) * mm});
            skLineSegment(sketch, "E61.17.11", {"start": v(-47.2, -98.65) * mm, "end": v(-45.97, -97.81) * mm});
            skArc(sketch, "E61.17.12", {"start": v(-50.45, -99.01) * mm, "mid": v(-48.92, -99.23) * mm, "end": v(-47.58, -98.46) * mm});
            skLineSegment(sketch, "E61.17.13", {"start": v(-47.6, -98.46) * mm, "end": v(-47.2, -98.65) * mm});
            skLineSegment(sketch, "E61.18.0", {"start": v(-17.5, -109.74) * mm, "end": v(-27.7, -115.08) * mm});
            skLineSegment(sketch, "E61.18.1", {"start": v(-34.34, -105.68) * mm, "end": v(-27.7, -115.08) * mm});
            skLineSegment(sketch, "E61.18.2", {"start": v(-25.35, -104.71) * mm, "end": v(-20.9, -105.78) * mm});
            skLineSegment(sketch, "E61.18.3", {"start": v(-19.91, -107.54) * mm, "end": v(-20.41, -106.13) * mm});
            skArc(sketch, "E61.18.4", {"start": v(-20.9, -105.78) * mm, "mid": v(-20.62, -105.9) * mm, "end": v(-20.41, -106.13) * mm});
            skLineSegment(sketch, "E61.18.5", {"start": v(-19.48, -107.6) * mm, "end": v(-19.91, -107.54) * mm});
            skArc(sketch, "E61.18.6", {"start": v(-17.5, -109.74) * mm, "mid": v(-18.86, -109.01) * mm, "end": v(-19.5, -107.6) * mm});
            skLineSegment(sketch, "E61.18.7", {"start": v(-19.5, -107.6) * mm, "end": v(-19.48, -107.6) * mm});
            skLineSegment(sketch, "E61.18.8", {"start": v(-19.5, -107.6) * mm, "end": v(-19.48, -107.6) * mm});
            skArc(sketch, "E61.18.9", {"start": v(-29.51, -103.7) * mm, "mid": v(-29.82, -103.7) * mm, "end": v(-30.1, -103.8) * mm});
            skLineSegment(sketch, "E61.18.10", {"start": v(-25.06, -104.78) * mm, "end": v(-29.51, -103.7) * mm});
            skLineSegment(sketch, "E61.18.11", {"start": v(-31.2, -104.82) * mm, "end": v(-30.1, -103.8) * mm});
            skArc(sketch, "E61.18.12", {"start": v(-34.34, -105.68) * mm, "mid": v(-32.8, -105.66) * mm, "end": v(-31.6, -104.7) * mm});
            skLineSegment(sketch, "E61.18.13", {"start": v(-31.6, -104.69) * mm, "end": v(-31.2, -104.82) * mm});
            skLineSegment(sketch, "E61.19.0", {"start": v(-0.12, -111.12) * mm, "end": v(-9.35, -118) * mm});
            skLineSegment(sketch, "E61.19.1", {"start": v(-17.38, -109.75) * mm, "end": v(-9.35, -118) * mm});
            skLineSegment(sketch, "E61.19.2", {"start": v(-8.66, -107.39) * mm, "end": v(-4.1, -107.75) * mm});
            skLineSegment(sketch, "E61.19.3", {"start": v(-2.85, -109.33) * mm, "end": v(-3.56, -108.02) * mm});
            skArc(sketch, "E61.19.4", {"start": v(-4.1, -107.75) * mm, "mid": v(-3.8, -107.83) * mm, "end": v(-3.56, -108.02) * mm});
            skLineSegment(sketch, "E61.19.5", {"start": v(-2.4, -109.33) * mm, "end": v(-2.85, -109.33) * mm});
            skArc(sketch, "E61.19.6", {"start": v(-0.12, -111.12) * mm, "mid": v(-1.58, -110.62) * mm, "end": v(-2.42, -109.33) * mm});
            skLineSegment(sketch, "E61.19.7", {"start": v(-2.42, -109.33) * mm, "end": v(-2.4, -109.33) * mm});
            skLineSegment(sketch, "E61.19.8", {"start": v(-2.42, -109.33) * mm, "end": v(-2.4, -109.33) * mm});
            skArc(sketch, "E61.19.9", {"start": v(-12.93, -107.05) * mm, "mid": v(-13.23, -107.08) * mm, "end": v(-13.5, -107.23) * mm});
            skLineSegment(sketch, "E61.19.10", {"start": v(-8.36, -107.41) * mm, "end": v(-12.93, -107.05) * mm});
            skLineSegment(sketch, "E61.19.11", {"start": v(-14.4, -108.41) * mm, "end": v(-13.5, -107.23) * mm});
            skArc(sketch, "E61.19.12", {"start": v(-17.38, -109.75) * mm, "mid": v(-15.86, -109.49) * mm, "end": v(-14.82, -108.35) * mm});
            skLineSegment(sketch, "E61.19.13", {"start": v(-14.84, -108.34) * mm, "end": v(-14.4, -108.41) * mm});
            skLineSegment(sketch, "E61.20.0", {"start": v(17.27, -109.77) * mm, "end": v(9.22, -118) * mm});
            skLineSegment(sketch, "E61.20.1", {"start": v(0, -111.12) * mm, "end": v(9.22, -118) * mm});
            skLineSegment(sketch, "E61.20.2", {"start": v(8.25, -107.42) * mm, "end": v(12.81, -107.06) * mm});
            skLineSegment(sketch, "E61.20.3", {"start": v(14.3, -108.43) * mm, "end": v(13.38, -107.24) * mm});
            skArc(sketch, "E61.20.4", {"start": v(12.81, -107.06) * mm, "mid": v(13.11, -107.1) * mm, "end": v(13.38, -107.24) * mm});
            skLineSegment(sketch, "E61.20.5", {"start": v(14.73, -108.36) * mm, "end": v(14.3, -108.43) * mm});
            skArc(sketch, "E61.20.6", {"start": v(17.27, -109.77) * mm, "mid": v(15.75, -109.5) * mm, "end": v(14.7, -108.36) * mm});
            skLineSegment(sketch, "E61.20.7", {"start": v(14.7, -108.36) * mm, "end": v(14.73, -108.36) * mm});
            skLineSegment(sketch, "E61.20.8", {"start": v(14.7, -108.36) * mm, "end": v(14.73, -108.36) * mm});
            skArc(sketch, "E61.20.9", {"start": v(3.98, -107.75) * mm, "mid": v(3.69, -107.83) * mm, "end": v(3.45, -108.02) * mm});
            skLineSegment(sketch, "E61.20.10", {"start": v(8.54, -107.4) * mm, "end": v(3.98, -107.75) * mm});
            skLineSegment(sketch, "E61.20.11", {"start": v(2.73, -109.33) * mm, "end": v(3.45, -108.02) * mm});
            skArc(sketch, "E61.20.12", {"start": v(0, -111.12) * mm, "mid": v(1.46, -110.62) * mm, "end": v(2.3, -109.33) * mm});
            skLineSegment(sketch, "E61.20.13", {"start": v(2.3, -109.33) * mm, "end": v(2.73, -109.33) * mm});
            skLineSegment(sketch, "E61.21.0", {"start": v(34.23, -105.72) * mm, "end": v(27.57, -115.11) * mm});
            skLineSegment(sketch, "E61.21.1", {"start": v(17.38, -109.75) * mm, "end": v(27.57, -115.11) * mm});
            skLineSegment(sketch, "E61.21.2", {"start": v(24.95, -104.8) * mm, "end": v(29.4, -103.74) * mm});
            skLineSegment(sketch, "E61.21.3", {"start": v(31.08, -104.86) * mm, "end": v(30, -103.83) * mm});
            skArc(sketch, "E61.21.4", {"start": v(29.4, -103.74) * mm, "mid": v(29.7, -103.73) * mm, "end": v(30, -103.83) * mm});
            skLineSegment(sketch, "E61.21.5", {"start": v(31.5, -104.72) * mm, "end": v(31.08, -104.86) * mm});
            skArc(sketch, "E61.21.6", {"start": v(34.23, -105.72) * mm, "mid": v(32.68, -105.7) * mm, "end": v(31.48, -104.73) * mm});
            skLineSegment(sketch, "E61.21.7", {"start": v(31.48, -104.73) * mm, "end": v(31.5, -104.72) * mm});
            skLineSegment(sketch, "E61.21.8", {"start": v(31.48, -104.73) * mm, "end": v(31.5, -104.72) * mm});
            skArc(sketch, "E61.21.9", {"start": v(20.79, -105.8) * mm, "mid": v(20.5, -105.93) * mm, "end": v(20.3, -106.15) * mm});
            skLineSegment(sketch, "E61.21.10", {"start": v(25.24, -104.74) * mm, "end": v(20.79, -105.8) * mm});
            skLineSegment(sketch, "E61.21.11", {"start": v(19.8, -107.56) * mm, "end": v(20.3, -106.15) * mm});
            skArc(sketch, "E61.21.12", {"start": v(17.38, -109.75) * mm, "mid": v(18.75, -109.03) * mm, "end": v(19.38, -107.63) * mm});
            skLineSegment(sketch, "E61.21.13", {"start": v(19.37, -107.63) * mm, "end": v(19.8, -107.56) * mm});
            skLineSegment(sketch, "E61.22.0", {"start": v(50.34, -99.07) * mm, "end": v(45.24, -109.38) * mm});
            skLineSegment(sketch, "E61.22.1", {"start": v(34.34, -105.68) * mm, "end": v(45.24, -109.38) * mm});
            skLineSegment(sketch, "E61.22.2", {"start": v(41.04, -99.61) * mm, "end": v(45.27, -97.86) * mm});
            skLineSegment(sketch, "E61.22.3", {"start": v(47.1, -98.7) * mm, "end": v(45.87, -97.86) * mm});
            skArc(sketch, "E61.22.4", {"start": v(45.27, -97.86) * mm, "mid": v(45.57, -97.8) * mm, "end": v(45.87, -97.86) * mm});
            skLineSegment(sketch, "E61.22.5", {"start": v(47.5, -98.5) * mm, "end": v(47.1, -98.7) * mm});
            skArc(sketch, "E61.22.6", {"start": v(50.34, -99.07) * mm, "mid": v(48.81, -99.28) * mm, "end": v(47.48, -98.51) * mm});
            skLineSegment(sketch, "E61.22.7", {"start": v(47.48, -98.51) * mm, "end": v(47.5, -98.5) * mm});
            skLineSegment(sketch, "E61.22.8", {"start": v(47.48, -98.51) * mm, "end": v(47.5, -98.5) * mm});
            skArc(sketch, "E61.22.9", {"start": v(37.08, -101.25) * mm, "mid": v(36.83, -101.42) * mm, "end": v(36.66, -101.67) * mm});
            skLineSegment(sketch, "E61.22.10", {"start": v(41.31, -99.5) * mm, "end": v(37.08, -101.25) * mm});
            skLineSegment(sketch, "E61.22.11", {"start": v(36.38, -103.14) * mm, "end": v(36.66, -101.67) * mm});
            skArc(sketch, "E61.22.12", {"start": v(34.34, -105.68) * mm, "mid": v(35.57, -104.76) * mm, "end": v(35.98, -103.27) * mm});
            skLineSegment(sketch, "E61.22.13", {"start": v(35.96, -103.27) * mm, "end": v(36.38, -103.14) * mm});
            skLineSegment(sketch, "E61.23.0", {"start": v(65.22, -89.97) * mm, "end": v(61.8, -100.96) * mm});
            skLineSegment(sketch, "E61.23.1", {"start": v(50.45, -99.01) * mm, "end": v(61.8, -100.96) * mm});
            skLineSegment(sketch, "E61.23.2", {"start": v(56.12, -91.97) * mm, "end": v(60.02, -89.58) * mm});
            skLineSegment(sketch, "E61.23.3", {"start": v(61.96, -90.12) * mm, "end": v(60.6, -89.48) * mm});
            skArc(sketch, "E61.23.4", {"start": v(60.02, -89.58) * mm, "mid": v(60.3, -89.47) * mm, "end": v(60.6, -89.48) * mm});
            skLineSegment(sketch, "E61.23.5", {"start": v(62.32, -89.86) * mm, "end": v(61.96, -90.12) * mm});
            skArc(sketch, "E61.23.6", {"start": v(65.22, -89.97) * mm, "mid": v(63.74, -90.42) * mm, "end": v(62.3, -89.87) * mm});
            skLineSegment(sketch, "E61.23.7", {"start": v(62.3, -89.87) * mm, "end": v(62.32, -89.86) * mm});
            skLineSegment(sketch, "E61.23.8", {"start": v(62.3, -89.87) * mm, "end": v(62.32, -89.86) * mm});
            skArc(sketch, "E61.23.9", {"start": v(52.46, -94.2) * mm, "mid": v(52.24, -94.4) * mm, "end": v(52.1, -94.68) * mm});
            skLineSegment(sketch, "E61.23.10", {"start": v(56.37, -91.81) * mm, "end": v(52.46, -94.2) * mm});
            skLineSegment(sketch, "E61.23.11", {"start": v(52.07, -96.18) * mm, "end": v(52.1, -94.68) * mm});
            skArc(sketch, "E61.23.12", {"start": v(50.45, -99.01) * mm, "mid": v(51.52, -97.9) * mm, "end": v(51.7, -96.37) * mm});
            skLineSegment(sketch, "E61.23.13", {"start": v(51.68, -96.38) * mm, "end": v(52.07, -96.18) * mm});
            skLineSegment(sketch, "E61.24.0", {"start": v(78.5, -78.66) * mm, "end": v(76.83, -90.05) * mm});
            skLineSegment(sketch, "E61.24.1", {"start": v(65.32, -89.9) * mm, "end": v(76.83, -90.05) * mm});
            skLineSegment(sketch, "E61.24.2", {"start": v(69.81, -82.06) * mm, "end": v(73.3, -79.08) * mm});
            skLineSegment(sketch, "E61.24.3", {"start": v(75.3, -79.32) * mm, "end": v(73.86, -78.9) * mm});
            skArc(sketch, "E61.24.4", {"start": v(73.3, -79.08) * mm, "mid": v(73.56, -78.94) * mm, "end": v(73.86, -78.9) * mm});
            skLineSegment(sketch, "E61.24.5", {"start": v(75.6, -79) * mm, "end": v(75.3, -79.32) * mm});
            skArc(sketch, "E61.24.6", {"start": v(78.5, -78.66) * mm, "mid": v(77.1, -79.34) * mm, "end": v(75.6, -79.02) * mm});
            skLineSegment(sketch, "E61.24.7", {"start": v(75.6, -79.02) * mm, "end": v(75.6, -79) * mm});
            skLineSegment(sketch, "E61.24.8", {"start": v(75.6, -79.02) * mm, "end": v(75.6, -79) * mm});
            skArc(sketch, "E61.24.9", {"start": v(66.55, -84.83) * mm, "mid": v(66.37, -85.07) * mm, "end": v(66.28, -85.36) * mm});
            skLineSegment(sketch, "E61.24.10", {"start": v(70.04, -81.86) * mm, "end": v(66.55, -84.83) * mm});
            skLineSegment(sketch, "E61.24.11", {"start": v(66.47, -86.85) * mm, "end": v(66.28, -85.36) * mm});
            skArc(sketch, "E61.24.12", {"start": v(65.32, -89.9) * mm, "mid": v(66.2, -88.64) * mm, "end": v(66.13, -87.1) * mm});
            skLineSegment(sketch, "E61.24.13", {"start": v(66.12, -87.1) * mm, "end": v(66.47, -86.85) * mm});
            skLineSegment(sketch, "E61.25.0", {"start": v(89.83, -65.41) * mm, "end": v(89.97, -76.92) * mm});
            skLineSegment(sketch, "E61.25.1", {"start": v(78.58, -78.58) * mm, "end": v(89.97, -76.92) * mm});
            skLineSegment(sketch, "E61.25.2", {"start": v(81.79, -70.13) * mm, "end": v(84.76, -66.65) * mm});
            skLineSegment(sketch, "E61.25.3", {"start": v(86.78, -66.56) * mm, "end": v(85.3, -66.37) * mm});
            skArc(sketch, "E61.25.4", {"start": v(84.76, -66.65) * mm, "mid": v(85, -66.46) * mm, "end": v(85.3, -66.37) * mm});
            skLineSegment(sketch, "E61.25.5", {"start": v(87.03, -66.2) * mm, "end": v(86.78, -66.56) * mm});
            skArc(sketch, "E61.25.6", {"start": v(89.83, -65.41) * mm, "mid": v(88.57, -66.3) * mm, "end": v(87.03, -66.22) * mm});
            skLineSegment(sketch, "E61.25.7", {"start": v(87.03, -66.22) * mm, "end": v(87.03, -66.2) * mm});
            skLineSegment(sketch, "E61.25.8", {"start": v(87.03, -66.22) * mm, "end": v(87.03, -66.2) * mm});
            skArc(sketch, "E61.25.9", {"start": v(79, -73.38) * mm, "mid": v(78.86, -73.64) * mm, "end": v(78.82, -73.95) * mm});
            skLineSegment(sketch, "E61.25.10", {"start": v(81.98, -69.9) * mm, "end": v(79, -73.38) * mm});
            skLineSegment(sketch, "E61.25.11", {"start": v(79.24, -75.38) * mm, "end": v(78.82, -73.95) * mm});
            skArc(sketch, "E61.25.12", {"start": v(78.58, -78.58) * mm, "mid": v(79.25, -77.19) * mm, "end": v(78.94, -75.68) * mm});
            skLineSegment(sketch, "E61.25.13", {"start": v(78.93, -75.7) * mm, "end": v(79.24, -75.38) * mm});
            skLineSegment(sketch, "E61.26.0", {"start": v(98.96, -50.55) * mm, "end": v(100.9, -61.9) * mm});
            skLineSegment(sketch, "E61.26.1", {"start": v(89.9, -65.32) * mm, "end": v(100.9, -61.9) * mm});
            skLineSegment(sketch, "E61.26.2", {"start": v(91.75, -56.47) * mm, "end": v(94.15, -52.56) * mm});
            skLineSegment(sketch, "E61.26.3", {"start": v(96.12, -52.17) * mm, "end": v(94.63, -52.21) * mm});
            skArc(sketch, "E61.26.4", {"start": v(94.15, -52.56) * mm, "mid": v(94.35, -52.34) * mm, "end": v(94.63, -52.21) * mm});
            skLineSegment(sketch, "E61.26.5", {"start": v(96.32, -51.78) * mm, "end": v(96.12, -52.17) * mm});
            skArc(sketch, "E61.26.6", {"start": v(98.96, -50.55) * mm, "mid": v(97.85, -51.63) * mm, "end": v(96.31, -51.8) * mm});
            skLineSegment(sketch, "E61.26.7", {"start": v(96.31, -51.8) * mm, "end": v(96.32, -51.78) * mm});
            skLineSegment(sketch, "E61.26.8", {"start": v(96.31, -51.8) * mm, "end": v(96.32, -51.78) * mm});
            skArc(sketch, "E61.26.9", {"start": v(89.51, -60.12) * mm, "mid": v(89.4, -60.4) * mm, "end": v(89.41, -60.7) * mm});
            skLineSegment(sketch, "E61.26.10", {"start": v(91.9, -56.21) * mm, "end": v(89.51, -60.12) * mm});
            skLineSegment(sketch, "E61.26.11", {"start": v(90.06, -62.06) * mm, "end": v(89.41, -60.7) * mm});
            skArc(sketch, "E61.26.12", {"start": v(89.9, -65.32) * mm, "mid": v(90.35, -63.84) * mm, "end": v(89.8, -62.4) * mm});
            skLineSegment(sketch, "E61.26.13", {"start": v(89.8, -62.41) * mm, "end": v(90.06, -62.06) * mm});
            skLineSegment(sketch, "E61.27.0", {"start": v(105.65, -34.45) * mm, "end": v(109.33, -45.36) * mm});
            skLineSegment(sketch, "E61.27.1", {"start": v(99.01, -50.45) * mm, "end": v(109.33, -45.36) * mm});
            skLineSegment(sketch, "E61.27.2", {"start": v(99.46, -41.42) * mm, "end": v(101.2, -37.2) * mm});
            skLineSegment(sketch, "E61.27.3", {"start": v(103.1, -36.5) * mm, "end": v(101.63, -36.77) * mm});
            skArc(sketch, "E61.27.4", {"start": v(101.2, -37.2) * mm, "mid": v(101.38, -36.94) * mm, "end": v(101.63, -36.77) * mm});
            skLineSegment(sketch, "E61.27.5", {"start": v(103.24, -36.07) * mm, "end": v(103.1, -36.5) * mm});
            skArc(sketch, "E61.27.6", {"start": v(105.65, -34.45) * mm, "mid": v(104.72, -35.68) * mm, "end": v(103.23, -36.09) * mm});
            skLineSegment(sketch, "E61.27.7", {"start": v(103.23, -36.09) * mm, "end": v(103.24, -36.07) * mm});
            skLineSegment(sketch, "E61.27.8", {"start": v(103.23, -36.09) * mm, "end": v(103.24, -36.07) * mm});
            skArc(sketch, "E61.27.9", {"start": v(97.82, -45.37) * mm, "mid": v(97.75, -45.67) * mm, "end": v(97.81, -45.97) * mm});
            skLineSegment(sketch, "E61.27.10", {"start": v(99.57, -41.14) * mm, "end": v(97.82, -45.37) * mm});
            skLineSegment(sketch, "E61.27.11", {"start": v(98.65, -47.2) * mm, "end": v(97.81, -45.97) * mm});
            skArc(sketch, "E61.27.12", {"start": v(99.01, -50.45) * mm, "mid": v(99.23, -48.92) * mm, "end": v(98.46, -47.58) * mm});
            skLineSegment(sketch, "E61.27.13", {"start": v(98.46, -47.6) * mm, "end": v(98.65, -47.2) * mm});
            skLineSegment(sketch, "E61.28.0", {"start": v(109.74, -17.5) * mm, "end": v(115.08, -27.7) * mm});
            skLineSegment(sketch, "E61.28.1", {"start": v(105.68, -34.34) * mm, "end": v(115.08, -27.7) * mm});
            skLineSegment(sketch, "E61.28.2", {"start": v(104.71, -25.35) * mm, "end": v(105.78, -20.9) * mm});
            skLineSegment(sketch, "E61.28.3", {"start": v(107.54, -19.91) * mm, "end": v(106.13, -20.41) * mm});
            skArc(sketch, "E61.28.4", {"start": v(105.78, -20.9) * mm, "mid": v(105.9, -20.62) * mm, "end": v(106.13, -20.41) * mm});
            skLineSegment(sketch, "E61.28.5", {"start": v(107.6, -19.48) * mm, "end": v(107.54, -19.91) * mm});
            skArc(sketch, "E61.28.6", {"start": v(109.74, -17.5) * mm, "mid": v(109.01, -18.86) * mm, "end": v(107.6, -19.5) * mm});
            skLineSegment(sketch, "E61.28.7", {"start": v(107.6, -19.5) * mm, "end": v(107.6, -19.48) * mm});
            skLineSegment(sketch, "E61.28.8", {"start": v(107.6, -19.5) * mm, "end": v(107.6, -19.48) * mm});
            skArc(sketch, "E61.28.9", {"start": v(103.7, -29.51) * mm, "mid": v(103.7, -29.82) * mm, "end": v(103.8, -30.1) * mm});
            skLineSegment(sketch, "E61.28.10", {"start": v(104.78, -25.06) * mm, "end": v(103.7, -29.51) * mm});
            skLineSegment(sketch, "E61.28.11", {"start": v(104.82, -31.2) * mm, "end": v(103.8, -30.1) * mm});
            skArc(sketch, "E61.28.12", {"start": v(105.68, -34.34) * mm, "mid": v(105.66, -32.8) * mm, "end": v(104.7, -31.6) * mm});
            skLineSegment(sketch, "E61.28.13", {"start": v(104.69, -31.6) * mm, "end": v(104.82, -31.2) * mm});
            skLineSegment(sketch, "E61.29.0", {"start": v(111.12, -0.12) * mm, "end": v(118, -9.35) * mm});
            skLineSegment(sketch, "E61.29.1", {"start": v(109.75, -17.38) * mm, "end": v(118, -9.35) * mm});
            skLineSegment(sketch, "E61.29.2", {"start": v(107.39, -8.66) * mm, "end": v(107.75, -4.1) * mm});
            skLineSegment(sketch, "E61.29.3", {"start": v(109.33, -2.85) * mm, "end": v(108.02, -3.56) * mm});
            skArc(sketch, "E61.29.4", {"start": v(107.75, -4.1) * mm, "mid": v(107.83, -3.8) * mm, "end": v(108.02, -3.56) * mm});
            skLineSegment(sketch, "E61.29.5", {"start": v(109.33, -2.4) * mm, "end": v(109.33, -2.85) * mm});
            skArc(sketch, "E61.29.6", {"start": v(111.12, -0.12) * mm, "mid": v(110.62, -1.58) * mm, "end": v(109.33, -2.42) * mm});
            skLineSegment(sketch, "E61.29.7", {"start": v(109.33, -2.42) * mm, "end": v(109.33, -2.4) * mm});
            skLineSegment(sketch, "E61.29.8", {"start": v(109.33, -2.42) * mm, "end": v(109.33, -2.4) * mm});
            skArc(sketch, "E61.29.9", {"start": v(107.05, -12.93) * mm, "mid": v(107.08, -13.23) * mm, "end": v(107.23, -13.5) * mm});
            skLineSegment(sketch, "E61.29.10", {"start": v(107.41, -8.36) * mm, "end": v(107.05, -12.93) * mm});
            skLineSegment(sketch, "E61.29.11", {"start": v(108.41, -14.4) * mm, "end": v(107.23, -13.5) * mm});
            skArc(sketch, "E61.29.12", {"start": v(109.75, -17.38) * mm, "mid": v(109.49, -15.86) * mm, "end": v(108.35, -14.82) * mm});
            skLineSegment(sketch, "E61.29.13", {"start": v(108.34, -14.84) * mm, "end": v(108.41, -14.4) * mm});
            skLineSegment(sketch, "E61.30.0", {"start": v(109.77, 17.27) * mm, "end": v(118, 9.22) * mm});
            skLineSegment(sketch, "E61.30.1", {"start": v(111.12, 0) * mm, "end": v(118, 9.22) * mm});
            skLineSegment(sketch, "E61.30.2", {"start": v(107.42, 8.25) * mm, "end": v(107.06, 12.81) * mm});
            skLineSegment(sketch, "E61.30.3", {"start": v(108.43, 14.3) * mm, "end": v(107.24, 13.38) * mm});
            skArc(sketch, "E61.30.4", {"start": v(107.06, 12.81) * mm, "mid": v(107.1, 13.11) * mm, "end": v(107.24, 13.38) * mm});
            skLineSegment(sketch, "E61.30.5", {"start": v(108.36, 14.73) * mm, "end": v(108.43, 14.3) * mm});
            skArc(sketch, "E61.30.6", {"start": v(109.77, 17.27) * mm, "mid": v(109.5, 15.75) * mm, "end": v(108.36, 14.7) * mm});
            skLineSegment(sketch, "E61.30.7", {"start": v(108.36, 14.7) * mm, "end": v(108.36, 14.73) * mm});
            skLineSegment(sketch, "E61.30.8", {"start": v(108.36, 14.7) * mm, "end": v(108.36, 14.73) * mm});
            skArc(sketch, "E61.30.9", {"start": v(107.75, 3.98) * mm, "mid": v(107.83, 3.69) * mm, "end": v(108.02, 3.45) * mm});
            skLineSegment(sketch, "E61.30.10", {"start": v(107.4, 8.54) * mm, "end": v(107.75, 3.98) * mm});
            skLineSegment(sketch, "E61.30.11", {"start": v(109.33, 2.73) * mm, "end": v(108.02, 3.45) * mm});
            skArc(sketch, "E61.30.12", {"start": v(111.12, 0) * mm, "mid": v(110.62, 1.46) * mm, "end": v(109.33, 2.3) * mm});
            skLineSegment(sketch, "E61.30.13", {"start": v(109.33, 2.3) * mm, "end": v(109.33, 2.73) * mm});
            skLineSegment(sketch, "E61.31.0", {"start": v(105.72, 34.23) * mm, "end": v(115.11, 27.57) * mm});
            skLineSegment(sketch, "E61.31.1", {"start": v(109.75, 17.38) * mm, "end": v(115.11, 27.57) * mm});
            skLineSegment(sketch, "E61.31.2", {"start": v(104.8, 24.95) * mm, "end": v(103.74, 29.4) * mm});
            skLineSegment(sketch, "E61.31.3", {"start": v(104.86, 31.08) * mm, "end": v(103.83, 30) * mm});
            skArc(sketch, "E61.31.4", {"start": v(103.74, 29.4) * mm, "mid": v(103.73, 29.7) * mm, "end": v(103.83, 30) * mm});
            skLineSegment(sketch, "E61.31.5", {"start": v(104.72, 31.5) * mm, "end": v(104.86, 31.08) * mm});
            skArc(sketch, "E61.31.6", {"start": v(105.72, 34.23) * mm, "mid": v(105.7, 32.68) * mm, "end": v(104.73, 31.48) * mm});
            skLineSegment(sketch, "E61.31.7", {"start": v(104.73, 31.48) * mm, "end": v(104.72, 31.5) * mm});
            skLineSegment(sketch, "E61.31.8", {"start": v(104.73, 31.48) * mm, "end": v(104.72, 31.5) * mm});
            skArc(sketch, "E61.31.9", {"start": v(105.8, 20.79) * mm, "mid": v(105.93, 20.5) * mm, "end": v(106.15, 20.3) * mm});
            skLineSegment(sketch, "E61.31.10", {"start": v(104.74, 25.24) * mm, "end": v(105.8, 20.79) * mm});
            skLineSegment(sketch, "E61.31.11", {"start": v(107.56, 19.8) * mm, "end": v(106.15, 20.3) * mm});
            skArc(sketch, "E61.31.12", {"start": v(109.75, 17.38) * mm, "mid": v(109.03, 18.75) * mm, "end": v(107.63, 19.38) * mm});
            skLineSegment(sketch, "E61.31.13", {"start": v(107.63, 19.37) * mm, "end": v(107.56, 19.8) * mm});
            skLineSegment(sketch, "E61.32.0", {"start": v(99.07, 50.34) * mm, "end": v(109.38, 45.24) * mm});
            skLineSegment(sketch, "E61.32.1", {"start": v(105.68, 34.34) * mm, "end": v(109.38, 45.24) * mm});
            skLineSegment(sketch, "E61.32.2", {"start": v(99.61, 41.04) * mm, "end": v(97.86, 45.27) * mm});
            skLineSegment(sketch, "E61.32.3", {"start": v(98.7, 47.1) * mm, "end": v(97.86, 45.87) * mm});
            skArc(sketch, "E61.32.4", {"start": v(97.86, 45.27) * mm, "mid": v(97.8, 45.57) * mm, "end": v(97.86, 45.87) * mm});
            skLineSegment(sketch, "E61.32.5", {"start": v(98.5, 47.5) * mm, "end": v(98.7, 47.1) * mm});
            skArc(sketch, "E61.32.6", {"start": v(99.07, 50.34) * mm, "mid": v(99.28, 48.81) * mm, "end": v(98.51, 47.48) * mm});
            skLineSegment(sketch, "E61.32.7", {"start": v(98.51, 47.48) * mm, "end": v(98.5, 47.5) * mm});
            skLineSegment(sketch, "E61.32.8", {"start": v(98.51, 47.48) * mm, "end": v(98.5, 47.5) * mm});
            skArc(sketch, "E61.32.9", {"start": v(101.25, 37.08) * mm, "mid": v(101.42, 36.83) * mm, "end": v(101.67, 36.66) * mm});
            skLineSegment(sketch, "E61.32.10", {"start": v(99.5, 41.31) * mm, "end": v(101.25, 37.08) * mm});
            skLineSegment(sketch, "E61.32.11", {"start": v(103.14, 36.38) * mm, "end": v(101.67, 36.66) * mm});
            skArc(sketch, "E61.32.12", {"start": v(105.68, 34.34) * mm, "mid": v(104.76, 35.57) * mm, "end": v(103.27, 35.98) * mm});
            skLineSegment(sketch, "E61.32.13", {"start": v(103.27, 35.96) * mm, "end": v(103.14, 36.38) * mm});
            skLineSegment(sketch, "E61.33.0", {"start": v(89.97, 65.22) * mm, "end": v(100.96, 61.8) * mm});
            skLineSegment(sketch, "E61.33.1", {"start": v(99.01, 50.45) * mm, "end": v(100.96, 61.8) * mm});
            skLineSegment(sketch, "E61.33.2", {"start": v(91.97, 56.12) * mm, "end": v(89.58, 60.02) * mm});
            skLineSegment(sketch, "E61.33.3", {"start": v(90.12, 61.96) * mm, "end": v(89.48, 60.6) * mm});
            skArc(sketch, "E61.33.4", {"start": v(89.58, 60.02) * mm, "mid": v(89.47, 60.3) * mm, "end": v(89.48, 60.6) * mm});
            skLineSegment(sketch, "E61.33.5", {"start": v(89.86, 62.32) * mm, "end": v(90.12, 61.96) * mm});
            skArc(sketch, "E61.33.6", {"start": v(89.97, 65.22) * mm, "mid": v(90.42, 63.74) * mm, "end": v(89.87, 62.3) * mm});
            skLineSegment(sketch, "E61.33.7", {"start": v(89.87, 62.3) * mm, "end": v(89.86, 62.32) * mm});
            skLineSegment(sketch, "E61.33.8", {"start": v(89.87, 62.3) * mm, "end": v(89.86, 62.32) * mm});
            skArc(sketch, "E61.33.9", {"start": v(94.2, 52.46) * mm, "mid": v(94.4, 52.24) * mm, "end": v(94.68, 52.1) * mm});
            skLineSegment(sketch, "E61.33.10", {"start": v(91.81, 56.37) * mm, "end": v(94.2, 52.46) * mm});
            skLineSegment(sketch, "E61.33.11", {"start": v(96.18, 52.07) * mm, "end": v(94.68, 52.1) * mm});
            skArc(sketch, "E61.33.12", {"start": v(99.01, 50.45) * mm, "mid": v(97.9, 51.52) * mm, "end": v(96.37, 51.7) * mm});
            skLineSegment(sketch, "E61.33.13", {"start": v(96.38, 51.68) * mm, "end": v(96.18, 52.07) * mm});
            skLineSegment(sketch, "E61.34.0", {"start": v(78.66, 78.5) * mm, "end": v(90.05, 76.83) * mm});
            skLineSegment(sketch, "E61.34.1", {"start": v(89.9, 65.32) * mm, "end": v(90.05, 76.83) * mm});
            skLineSegment(sketch, "E61.34.2", {"start": v(82.06, 69.81) * mm, "end": v(79.08, 73.3) * mm});
            skLineSegment(sketch, "E61.34.3", {"start": v(79.32, 75.3) * mm, "end": v(78.9, 73.86) * mm});
            skArc(sketch, "E61.34.4", {"start": v(79.08, 73.3) * mm, "mid": v(78.94, 73.56) * mm, "end": v(78.9, 73.86) * mm});
            skLineSegment(sketch, "E61.34.5", {"start": v(79, 75.6) * mm, "end": v(79.32, 75.3) * mm});
            skArc(sketch, "E61.34.6", {"start": v(78.66, 78.5) * mm, "mid": v(79.34, 77.1) * mm, "end": v(79.02, 75.6) * mm});
            skLineSegment(sketch, "E61.34.7", {"start": v(79.02, 75.6) * mm, "end": v(79, 75.6) * mm});
            skLineSegment(sketch, "E61.34.8", {"start": v(79.02, 75.6) * mm, "end": v(79, 75.6) * mm});
            skArc(sketch, "E61.34.9", {"start": v(84.83, 66.55) * mm, "mid": v(85.07, 66.37) * mm, "end": v(85.36, 66.28) * mm});
            skLineSegment(sketch, "E61.34.10", {"start": v(81.86, 70.04) * mm, "end": v(84.83, 66.55) * mm});
            skLineSegment(sketch, "E61.34.11", {"start": v(86.85, 66.47) * mm, "end": v(85.36, 66.28) * mm});
            skArc(sketch, "E61.34.12", {"start": v(89.9, 65.32) * mm, "mid": v(88.64, 66.2) * mm, "end": v(87.1, 66.13) * mm});
            skLineSegment(sketch, "E61.34.13", {"start": v(87.1, 66.12) * mm, "end": v(86.85, 66.47) * mm});
            skLineSegment(sketch, "E61.35.0", {"start": v(65.41, 89.83) * mm, "end": v(76.92, 89.97) * mm});
            skLineSegment(sketch, "E61.35.1", {"start": v(78.58, 78.58) * mm, "end": v(76.92, 89.97) * mm});
            skLineSegment(sketch, "E61.35.2", {"start": v(70.13, 81.79) * mm, "end": v(66.65, 84.76) * mm});
            skLineSegment(sketch, "E61.35.3", {"start": v(66.56, 86.78) * mm, "end": v(66.37, 85.3) * mm});
            skArc(sketch, "E61.35.4", {"start": v(66.65, 84.76) * mm, "mid": v(66.46, 85) * mm, "end": v(66.37, 85.3) * mm});
            skLineSegment(sketch, "E61.35.5", {"start": v(66.2, 87.03) * mm, "end": v(66.56, 86.78) * mm});
            skArc(sketch, "E61.35.6", {"start": v(65.41, 89.83) * mm, "mid": v(66.3, 88.57) * mm, "end": v(66.22, 87.03) * mm});
            skLineSegment(sketch, "E61.35.7", {"start": v(66.22, 87.03) * mm, "end": v(66.2, 87.03) * mm});
            skLineSegment(sketch, "E61.35.8", {"start": v(66.22, 87.03) * mm, "end": v(66.2, 87.03) * mm});
            skArc(sketch, "E61.35.9", {"start": v(73.38, 79) * mm, "mid": v(73.64, 78.86) * mm, "end": v(73.95, 78.82) * mm});
            skLineSegment(sketch, "E61.35.10", {"start": v(69.9, 81.98) * mm, "end": v(73.38, 79) * mm});
            skLineSegment(sketch, "E61.35.11", {"start": v(75.38, 79.24) * mm, "end": v(73.95, 78.82) * mm});
            skArc(sketch, "E61.35.12", {"start": v(78.58, 78.58) * mm, "mid": v(77.19, 79.25) * mm, "end": v(75.68, 78.94) * mm});
            skLineSegment(sketch, "E61.35.13", {"start": v(75.7, 78.93) * mm, "end": v(75.38, 79.24) * mm});
            skLineSegment(sketch, "E61.36.0", {"start": v(50.55, 98.96) * mm, "end": v(61.9, 100.9) * mm});
            skLineSegment(sketch, "E61.36.1", {"start": v(65.32, 89.9) * mm, "end": v(61.9, 100.9) * mm});
            skLineSegment(sketch, "E61.36.2", {"start": v(56.47, 91.75) * mm, "end": v(52.56, 94.15) * mm});
            skLineSegment(sketch, "E61.36.3", {"start": v(52.17, 96.12) * mm, "end": v(52.21, 94.63) * mm});
            skArc(sketch, "E61.36.4", {"start": v(52.56, 94.15) * mm, "mid": v(52.34, 94.35) * mm, "end": v(52.21, 94.63) * mm});
            skLineSegment(sketch, "E61.36.5", {"start": v(51.78, 96.32) * mm, "end": v(52.17, 96.12) * mm});
            skArc(sketch, "E61.36.6", {"start": v(50.55, 98.96) * mm, "mid": v(51.63, 97.85) * mm, "end": v(51.8, 96.31) * mm});
            skLineSegment(sketch, "E61.36.7", {"start": v(51.8, 96.31) * mm, "end": v(51.78, 96.32) * mm});
            skLineSegment(sketch, "E61.36.8", {"start": v(51.8, 96.31) * mm, "end": v(51.78, 96.32) * mm});
            skArc(sketch, "E61.36.9", {"start": v(60.12, 89.51) * mm, "mid": v(60.4, 89.4) * mm, "end": v(60.7, 89.41) * mm});
            skLineSegment(sketch, "E61.36.10", {"start": v(56.21, 91.9) * mm, "end": v(60.12, 89.51) * mm});
            skLineSegment(sketch, "E61.36.11", {"start": v(62.06, 90.06) * mm, "end": v(60.7, 89.41) * mm});
            skArc(sketch, "E61.36.12", {"start": v(65.32, 89.9) * mm, "mid": v(63.84, 90.35) * mm, "end": v(62.4, 89.8) * mm});
            skLineSegment(sketch, "E61.36.13", {"start": v(62.41, 89.8) * mm, "end": v(62.06, 90.06) * mm});
            skLineSegment(sketch, "E61.37.0", {"start": v(34.45, 105.65) * mm, "end": v(45.36, 109.33) * mm});
            skLineSegment(sketch, "E61.37.1", {"start": v(50.45, 99.01) * mm, "end": v(45.36, 109.33) * mm});
            skLineSegment(sketch, "E61.37.2", {"start": v(41.42, 99.46) * mm, "end": v(37.2, 101.2) * mm});
            skLineSegment(sketch, "E61.37.3", {"start": v(36.5, 103.1) * mm, "end": v(36.77, 101.63) * mm});
            skArc(sketch, "E61.37.4", {"start": v(37.2, 101.2) * mm, "mid": v(36.94, 101.38) * mm, "end": v(36.77, 101.63) * mm});
            skLineSegment(sketch, "E61.37.5", {"start": v(36.07, 103.24) * mm, "end": v(36.5, 103.1) * mm});
            skArc(sketch, "E61.37.6", {"start": v(34.45, 105.65) * mm, "mid": v(35.68, 104.72) * mm, "end": v(36.09, 103.23) * mm});
            skLineSegment(sketch, "E61.37.7", {"start": v(36.09, 103.23) * mm, "end": v(36.07, 103.24) * mm});
            skLineSegment(sketch, "E61.37.8", {"start": v(36.09, 103.23) * mm, "end": v(36.07, 103.24) * mm});
            skArc(sketch, "E61.37.9", {"start": v(45.37, 97.82) * mm, "mid": v(45.67, 97.75) * mm, "end": v(45.97, 97.81) * mm});
            skLineSegment(sketch, "E61.37.10", {"start": v(41.14, 99.57) * mm, "end": v(45.37, 97.82) * mm});
            skLineSegment(sketch, "E61.37.11", {"start": v(47.2, 98.65) * mm, "end": v(45.97, 97.81) * mm});
            skArc(sketch, "E61.37.12", {"start": v(50.45, 99.01) * mm, "mid": v(48.92, 99.23) * mm, "end": v(47.58, 98.46) * mm});
            skLineSegment(sketch, "E61.37.13", {"start": v(47.6, 98.46) * mm, "end": v(47.2, 98.65) * mm});
            skLineSegment(sketch, "E61.38.0", {"start": v(17.5, 109.74) * mm, "end": v(27.7, 115.08) * mm});
            skLineSegment(sketch, "E61.38.1", {"start": v(34.34, 105.68) * mm, "end": v(27.7, 115.08) * mm});
            skLineSegment(sketch, "E61.38.2", {"start": v(25.35, 104.71) * mm, "end": v(20.9, 105.78) * mm});
            skLineSegment(sketch, "E61.38.3", {"start": v(19.91, 107.54) * mm, "end": v(20.41, 106.13) * mm});
            skArc(sketch, "E61.38.4", {"start": v(20.9, 105.78) * mm, "mid": v(20.62, 105.9) * mm, "end": v(20.41, 106.13) * mm});
            skLineSegment(sketch, "E61.38.5", {"start": v(19.48, 107.6) * mm, "end": v(19.91, 107.54) * mm});
            skArc(sketch, "E61.38.6", {"start": v(17.5, 109.74) * mm, "mid": v(18.86, 109.01) * mm, "end": v(19.5, 107.6) * mm});
            skLineSegment(sketch, "E61.38.7", {"start": v(19.5, 107.6) * mm, "end": v(19.48, 107.6) * mm});
            skLineSegment(sketch, "E61.38.8", {"start": v(19.5, 107.6) * mm, "end": v(19.48, 107.6) * mm});
            skArc(sketch, "E61.38.9", {"start": v(29.51, 103.7) * mm, "mid": v(29.82, 103.7) * mm, "end": v(30.1, 103.8) * mm});
            skLineSegment(sketch, "E61.38.10", {"start": v(25.06, 104.78) * mm, "end": v(29.51, 103.7) * mm});
            skLineSegment(sketch, "E61.38.11", {"start": v(31.2, 104.82) * mm, "end": v(30.1, 103.8) * mm});
            skArc(sketch, "E61.38.12", {"start": v(34.34, 105.68) * mm, "mid": v(32.8, 105.66) * mm, "end": v(31.6, 104.7) * mm});
            skLineSegment(sketch, "E61.38.13", {"start": v(31.6, 104.69) * mm, "end": v(31.2, 104.82) * mm});
            skLineSegment(sketch, "E61.39.0", {"start": v(0.12, 111.12) * mm, "end": v(9.35, 118) * mm});
            skLineSegment(sketch, "E61.39.1", {"start": v(17.38, 109.75) * mm, "end": v(9.35, 118) * mm});
            skLineSegment(sketch, "E61.39.2", {"start": v(8.66, 107.39) * mm, "end": v(4.1, 107.75) * mm});
            skLineSegment(sketch, "E61.39.3", {"start": v(2.85, 109.33) * mm, "end": v(3.56, 108.02) * mm});
            skArc(sketch, "E61.39.4", {"start": v(4.1, 107.75) * mm, "mid": v(3.8, 107.83) * mm, "end": v(3.56, 108.02) * mm});
            skLineSegment(sketch, "E61.39.5", {"start": v(2.4, 109.33) * mm, "end": v(2.85, 109.33) * mm});
            skArc(sketch, "E61.39.6", {"start": v(0.12, 111.12) * mm, "mid": v(1.58, 110.62) * mm, "end": v(2.42, 109.33) * mm});
            skLineSegment(sketch, "E61.39.7", {"start": v(2.42, 109.33) * mm, "end": v(2.4, 109.33) * mm});
            skLineSegment(sketch, "E61.39.8", {"start": v(2.42, 109.33) * mm, "end": v(2.4, 109.33) * mm});
            skArc(sketch, "E61.39.9", {"start": v(12.93, 107.05) * mm, "mid": v(13.23, 107.08) * mm, "end": v(13.5, 107.23) * mm});
            skLineSegment(sketch, "E61.39.10", {"start": v(8.36, 107.41) * mm, "end": v(12.93, 107.05) * mm});
            skLineSegment(sketch, "E61.39.11", {"start": v(14.4, 108.41) * mm, "end": v(13.5, 107.23) * mm});
            skArc(sketch, "E61.39.12", {"start": v(17.38, 109.75) * mm, "mid": v(15.86, 109.49) * mm, "end": v(14.82, 108.35) * mm});
            skLineSegment(sketch, "E61.39.13", {"start": v(14.84, 108.34) * mm, "end": v(14.4, 108.41) * mm});
            skSolve(sketch);
        }
        {
            var Q0;
            Q0=qSketchRegion(id+"F14",true);
            extrude(context, id + "F15", {"entities" : qUnion([Q0]), "operationType" : NewBodyOperationType.REMOVE, "depth" : 25.4 * mm});
        }
    });
